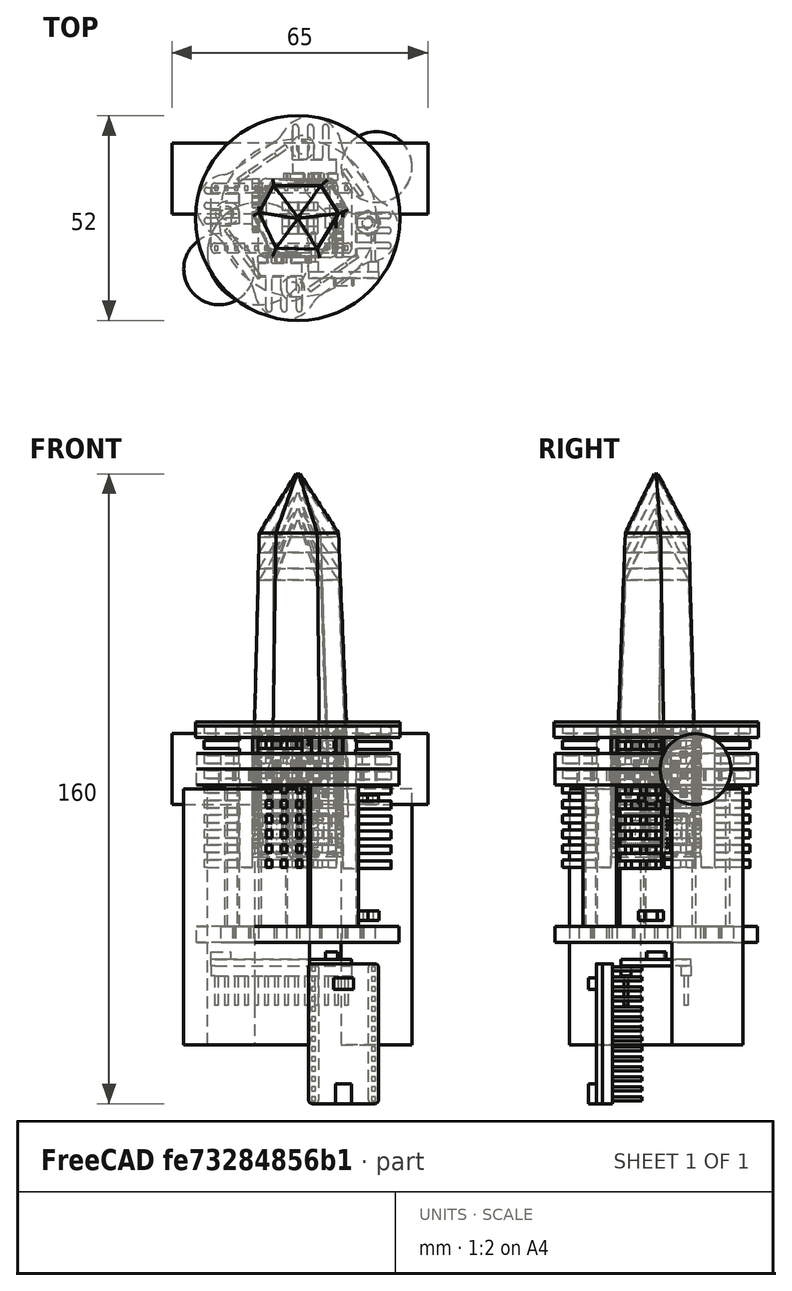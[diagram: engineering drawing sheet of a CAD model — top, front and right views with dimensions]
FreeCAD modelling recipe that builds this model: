
FCSTD DOCUMENT  (FreeCAD 0.18R16093 (Git))
Label: magic_crystal
License: All rights reserved
LicenseURL: http://en.wikipedia.org/wiki/All_rights_reserved
objects: PartDesign::Body×41, Sketcher::SketchObject×25, PartDesign::FeatureBase×25, TechDraw::DrawViewPart×18, PartDesign::Pad×13, App::Part×12, Part::Feature×11, TechDraw::DrawSVGTemplate×10, TechDraw::DrawPage×10, PartDesign::Pocket×6, PartDesign::Hole×6, PartDesign::PolarPattern×6, PartDesign::ShapeBinder×4, PartDesign::Boolean×4, App::DocumentObjectGroup×3, PartDesign::Mirrored×2, TechDraw::DrawViewDimension×2, Spreadsheet::Sheet×1, PartDesign::Fillet×1
note: 169 computed .brp shape members not serialized (recipe doc carries the construction recipe); baked Part::Feature solids carry a one-line shape summary decoded from their .brp

FEATURE [Part::Feature] COMPOUND176_copy_mp_cp001  label="LEDBoard_4x4_HD_simplified1"
  Placement = pos=(11.3,-4,0) rot=(0.57735,0.57735,-0.57735;2.0944rad)
  shape: bbox 2.65 x 13.6 x 33 mm, 1697 faces, 167 solids (baked)
FEATURE [Sketcher::SketchObject] Sketch003  label="lightguide_layer1_Sketch"
  MapMode = 5
  Placement = pos=(0,0,0) rot=(1,0,0;1.5708rad)
  Support = -> [XZ_Plane001]
  expr: Constraints[89] = data.led_height
  expr: Constraints[1] = data.lightguide_top_length
  expr: Constraints[86] = data.led_height
  expr: Constraints[20] = data.led_offset
  expr: Constraints[15] = data.led_pos_0
  expr: Constraints[21] = 5
  expr: Constraints[19] = data.led_offset
  expr: Constraints[18] = data.led_offset
  expr: Constraints[14] = data.led_height
  sketch-geometry (40):
    g0: LineSegment StartX=-4 StartY=0 StartZ=0 EndX=4 EndY=0 EndZ=0
    g1: LineSegment StartX=4.5 StartY=-8 StartZ=0 EndX=5 EndY=-8 EndZ=0
    g2: LineSegment StartX=5 StartY=-8 StartZ=0 EndX=5 EndY=-10 EndZ=0
    g3: LineSegment StartX=5 StartY=-10 StartZ=0 EndX=4.5 EndY=-10 EndZ=0
    g4: ArcOfCircle CenterX=4.5 CenterY=-7.9 CenterZ=0 NormalX=0 NormalY=0 NormalZ=1 AngleXU=0 Radius=2.1 StartAngle=3.14159 EndAngle=4.71239
    g5: ArcOfCircle CenterX=4.5 CenterY=-7.5 CenterZ=0 NormalX=0 NormalY=0 NormalZ=1 AngleXU=0 Radius=0.5 StartAngle=3.14159 EndAngle=4.71239
    g6: LineSegment StartX=2.4 StartY=-7.9 StartZ=0 EndX=2.4 EndY=-2 EndZ=0
    g7: LineSegment StartX=4 StartY=-7.5 StartZ=0 EndX=4 EndY=0 EndZ=0
    g8: GeomPoint X=5 Y=-9 Z=0
    g9: GeomPoint X=5 Y=-14 Z=0
    g10: GeomPoint X=5 Y=-19 Z=0
    g11: GeomPoint X=5 Y=-24 Z=0
    g12: LineSegment StartX=4.5 StartY=-13 StartZ=0 EndX=5 EndY=-13 EndZ=0
    g13: LineSegment StartX=5 StartY=-13 StartZ=0 EndX=5 EndY=-15 EndZ=0
    g14: LineSegment StartX=5 StartY=-15 StartZ=0 EndX=4.5 EndY=-15 EndZ=0
    g15: ArcOfCircle CenterX=4.5 CenterY=-10.6 CenterZ=0 NormalX=0 NormalY=0 NormalZ=1 AngleXU=0 Radius=4.4 StartAngle=3.14159 EndAngle=4.71239
    g16: ArcOfCircle CenterX=4.5 CenterY=-10.7 CenterZ=0 NormalX=0 NormalY=0 NormalZ=1 AngleXU=0 Radius=2.3 StartAngle=3.14159 EndAngle=4.71239
    g17: LineSegment StartX=0.1 StartY=-10.6 StartZ=0 EndX=0.1 EndY=-2 EndZ=0
    g18: LineSegment StartX=2.2 StartY=-10.7 StartZ=0 EndX=2.2 EndY=-2 EndZ=0
    g19: ArcOfCircle CenterX=2.3 CenterY=-2 CenterZ=0 NormalX=0 NormalY=0 NormalZ=1 AngleXU=0 Radius=0.1 StartAngle=-9e-16 EndAngle=3.14159
    g20: LineSegment StartX=4 StartY=-18 StartZ=0 EndX=5 EndY=-18 EndZ=0
    g21: LineSegment StartX=5 StartY=-18 StartZ=0 EndX=5 EndY=-20 EndZ=0
    g22: LineSegment StartX=5 StartY=-20 StartZ=0 EndX=4 EndY=-20 EndZ=0
    g23: ArcOfCircle CenterX=4 CenterY=-13.8 CenterZ=0 NormalX=0 NormalY=0 NormalZ=1 AngleXU=0 Radius=6.2 StartAngle=3.14159 EndAngle=4.71239
    g24: ArcOfCircle CenterX=4 CenterY=-13.9 CenterZ=0 NormalX=0 NormalY=0 NormalZ=1 AngleXU=0 Radius=4.1 StartAngle=3.14159 EndAngle=4.71239
    g25: LineSegment StartX=-2.2 StartY=-13.8 StartZ=0 EndX=-2.2 EndY=-2 EndZ=0
    g26: LineSegment StartX=-0.1 StartY=-13.9 StartZ=0 EndX=-0.1 EndY=-2 EndZ=0
    g27: ArcOfCircle CenterX=0 CenterY=-2 CenterZ=0 NormalX=0 NormalY=0 NormalZ=1 AngleXU=0 Radius=0.1 StartAngle=-9e-16 EndAngle=3.14159
    g28: LineSegment StartX=4 StartY=-23 StartZ=0 EndX=5 EndY=-23 EndZ=0
    g29: LineSegment StartX=5 StartY=-23 StartZ=0 EndX=5 EndY=-25 EndZ=0
    g30: LineSegment StartX=5 StartY=-25 StartZ=0 EndX=4 EndY=-25 EndZ=0
    g31: ArcOfCircle CenterX=4 CenterY=-17 CenterZ=0 NormalX=0 NormalY=0 NormalZ=1 AngleXU=0 Radius=8 StartAngle=3.14159 EndAngle=4.71239
    g32: ArcOfCircle CenterX=4 CenterY=-16.6 CenterZ=0 NormalX=0 NormalY=0 NormalZ=1 AngleXU=0 Radius=6.4 StartAngle=3.14159 EndAngle=4.71239
    g33: LineSegment StartX=-4 StartY=-17 StartZ=0 EndX=-4 EndY=0 EndZ=0
    g34: LineSegment StartX=-2.4 StartY=-16.6 StartZ=0 EndX=-2.4 EndY=-2 EndZ=0
    g35: ArcOfCircle CenterX=-2.3 CenterY=-2 CenterZ=0 NormalX=0 NormalY=0 NormalZ=1 AngleXU=0 Radius=0.1 StartAngle=-9e-16 EndAngle=3.14159
    g36: LineSegment [constr] StartX=-4 StartY=-2 StartZ=0 EndX=-2.3 EndY=-2 EndZ=0
    g37: LineSegment [constr] StartX=-2.3 StartY=-2 StartZ=0 EndX=0 EndY=-2 EndZ=0
    g38: LineSegment [constr] StartX=0 StartY=-2 StartZ=0 EndX=2.3 EndY=-2 EndZ=0
    g39: LineSegment [constr] StartX=2.3 StartY=-2 StartZ=0 EndX=4 EndY=-2 EndZ=0
  constraints (100):
    c: Horizontal(g0)
    c: DistanceX(g0,g0) = 8
    c: Symmetric(g0,g0,g-1)
    c: Horizontal(g1)
    c: Coincident(g1,g2)
    c: Vertical(g2)
    c: Coincident(g2,g3)
    c: Horizontal(g3)
    c: Vertical(g6)
    c: Vertical(g7)
    c: Tangent(g5,g7) = 1.5708
    c: Tangent(g5,g1) = -1.5708
    c: Tangent(g4,g6) = 1.5708
    c: Tangent(g3,g4) = 1.5708
    c: DistanceY(g2,g2) = 2
    c: DistanceY(g8,g-1) = 9
    c: Symmetric(g2,g2,g8)
    c: Radius(g5) = 0.5
    c: DistanceY(g9,g8) = 5
    c: DistanceY(g10,g9) = 5
    c: DistanceY(g11,g10) = 5
    c: DistanceX(g8) = 5
    c: Coincident(g7,g0)
    c: PointOnObject(g9,g2)
    c: PointOnObject(g10,g2)
    c: PointOnObject(g11,g2)
    c: Horizontal(g12)
    c: Coincident(g12,g13)
    c: Vertical(g13)
    c: Coincident(g13,g14)
    c: Horizontal(g14)
    c: Vertical(g17)
    c: Vertical(g18)
    c: Tangent(g16,g18) = 1.5708
    c: Tangent(g16,g12) = -1.5708
    c: Tangent(g15,g17) = 1.5708
    c: Tangent(g14,g15) = 1.5708
    c: Symmetric(g13,g13,g9)
    c: Tangent(g6,g19) = -1.5708
    c: Radius(g19) = 0.1
    c: Tangent(g18,g19) = 1.5708
    c: Horizontal(g20)
    c: Coincident(g20,g21)
    c: Vertical(g21)
    c: Coincident(g21,g22)
    c: Horizontal(g22)
    c: Vertical(g25)
    c: Vertical(g26)
    c: Tangent(g24,g26) = 1.5708
    c: Tangent(g24,g20) = -1.5708
    c: Tangent(g23,g25) = 1.5708
    c: Tangent(g22,g23) = 1.5708
    c: Equal(g19,g27) = 0.1
    c: Tangent(g26,g27) = 1.5708
    c: Horizontal(g28)
    c: Coincident(g28,g29)
    c: Vertical(g29)
    c: Coincident(g29,g30)
    c: Horizontal(g30)
    c: Vertical(g33)
    c: Vertical(g34)
    c: Tangent(g32,g34) = 1.5708
    c: Tangent(g32,g28) = -1.5708
    c: Tangent(g31,g33) = 1.5708
    c: Tangent(g30,g31) = 1.5708
    c: Tangent(g34,g35) = 1.5708
    c: Symmetric(g21,g21,g10)
    c: Tangent(g35,g25) = -1.5708
    c: Tangent(g27,g17) = -1.5708
    c: Equal(g2,g21)
    c: Symmetric(g29,g29,g11)
    c: Coincident(g33,g0)
    c: Horizontal(g36)
    c: Coincident(g36,g37)
    c: Horizontal(g37)
    c: Coincident(g37,g38)
    c: Horizontal(g38)
    c: Coincident(g38,g39)
    c: Horizontal(g39)
    c: PointOnObject(g39,g7)
    c: PointOnObject(g36,g33)
    c: Coincident(g36,g35)
    c: Coincident(g27,g37)
    c: Coincident(g19,g38)
    c: DistanceY(g39,g-1) = 2
    c: DistanceX(g4,g5) = 1.6
    c: DistanceY(g29,g29) = 2
    c: Equal(g35,g19)
    c: DistanceX(g36,g34) = 1.6
    c: DistanceY(g13,g13) = 2
    c: PointOnObject(g27,g-2)
    c: DistanceX(g28,g28) = 1
    c: DistanceX(g20,g20) = 1
    c: Equal(g22,g20)
    c: Equal(g12,g14)
    c: Equal(g30,g28)
    c: Equal(g1,g3)
    c: DistanceX(g12,g12) = 0.5
    c: DistanceX(g1,g1) = 0.5
    c: DistanceX(g17,g18) = 2.1
FEATURE [PartDesign::Pad] Pad
  Length = 2
  Length2 = 100
  Midplane = true
  Placement = pos=(0,0,0) rot=(1,0,0;1.5708rad)
  Profile = -> Sketch003
  Refine = true
  Type = 0
  expr: Length = data.acrylglass_tchickness
FEATURE [PartDesign::Body] Body001  label="lightguide_layer1_Body"
  Group = -> [Sketch003,Pad]
  Origin = -> Origin001
  Placement = pos=(0,3,0) rot=(0,0,1;0rad)
  Tip = -> Pad
FEATURE [Sketcher::SketchObject] Sketch005  label="crystal_contour_simple_Sketch"
  MapMode = 5
  Support = -> [XY_Plane003]
  sketch-geometry (7):
    g0: LineSegment StartX=5 StartY=-8.66025 StartZ=0 EndX=10 EndY=-1.8e-15 EndZ=0
    g1: LineSegment StartX=10 StartY=-1.8e-15 StartZ=0 EndX=5 EndY=8.66025 EndZ=0
    g2: LineSegment StartX=5 StartY=8.66025 StartZ=0 EndX=-5 EndY=8.66025 EndZ=0
    g3: LineSegment StartX=-5 StartY=8.66025 StartZ=0 EndX=-10 EndY=1.8e-15 EndZ=0
    g4: LineSegment StartX=-10 StartY=1.8e-15 StartZ=0 EndX=-5 EndY=-8.66025 EndZ=0
    g5: LineSegment StartX=-5 StartY=-8.66025 StartZ=0 EndX=5 EndY=-8.66025 EndZ=0
    g6: Circle [constr] CenterX=0 CenterY=0 CenterZ=0 NormalX=0 NormalY=0 NormalZ=1 AngleXU=0 Radius=10
  constraints (16):
    c: Coincident(g0,g1)
    c: Coincident(g1,g2)
    c: Coincident(g2,g3)
    c: Coincident(g3,g4)
    c: Coincident(g4,g5)
    c: Coincident(g5,g0)
    c: Equal(g0, g1-g5) x5
    c: PointOnObject(g0,g6)
    c: PointOnObject(g1,g6)
    c: PointOnObject(g2,g6)
    c: PointOnObject(g3,g6)
    c: PointOnObject(g4,g6)
    c: PointOnObject(g5,g6)
    c: Coincident(g6,g-1)
    c: Horizontal(g5)
    c: Radius(g6) = 10
FEATURE [Part::Feature] COMPOUND176_copy_mp_cp002  label="LEDBoard_4x4_HD_simplified2"
  Placement = pos=(-4.1,-11.3,0) rot=(0.707107,0,-0.707107;3.14159rad)
  shape: bbox 13.6 x 2.65 x 33 mm, 1697 faces, 167 solids (baked)
FEATURE [Part::Feature] COMPOUND176_copy_mp_cp003  label="LEDBoard_4x4_HD_simplified3"
  Placement = pos=(-11.5,4,0) rot=(0.57735,-0.57735,-0.57735;4.18879rad)
  shape: bbox 2.65 x 13.6 x 33 mm, 1697 faces, 167 solids (baked)
FEATURE [Part::Feature] COMPOUND176_copy_mp_cp004  label="LEDBoard_4x4_HD_simplified4"
  Placement = pos=(4,11.3,0) rot=(0,1,0;1.5708rad)
  shape: bbox 13.6 x 2.65 x 33 mm, 1697 faces, 167 solids (baked)
FEATURE [Sketcher::SketchObject] Sketch006  label="lightguide_place1_Sketch"
  AttachmentOffset = pos=(4,-3,0) rot=(0,0,1;0rad)
  MapMode = 5
  Placement = pos=(4,-3,0) rot=(0,0,1;0rad)
  Support = -> [XY_Plane003]
  sketch-geometry (4):
    g0: LineSegment StartX=-3.15 StartY=4 StartZ=0 EndX=3.15 EndY=4 EndZ=0
    g1: LineSegment StartX=3.15 StartY=4 StartZ=0 EndX=3.15 EndY=-4 EndZ=0
    g2: LineSegment StartX=3.15 StartY=-4 StartZ=0 EndX=-3.15 EndY=-4 EndZ=0
    g3: LineSegment StartX=-3.15 StartY=-4 StartZ=0 EndX=-3.15 EndY=4 EndZ=0
  constraints (11):
    c: Coincident(g0,g1)
    c: Coincident(g1,g2)
    c: Coincident(g2,g3)
    c: Coincident(g3,g0)
    c: Horizontal(g0)
    c: Horizontal(g2)
    c: Vertical(g1)
    c: Vertical(g3)
    c: DistanceX(g0,g0) = 6.3
    c: Symmetric(g0,g2,g-1)
    c: DistanceY(g1,g1) = 8
FEATURE [Sketcher::SketchObject] Sketch007  label="lightguide_place2_Sketch"
  AttachmentOffset = pos=(-3.15,-3.85,0) rot=(0,0,1;1.5708rad)
  MapMode = 5
  Placement = pos=(-3.15,-3.85,0) rot=(0,0,1;1.5708rad)
  Support = -> [XY_Plane003]
  sketch-geometry (4):
    g0: LineSegment StartX=-3.15 StartY=4 StartZ=0 EndX=3.15 EndY=4 EndZ=0
    g1: LineSegment StartX=3.15 StartY=4 StartZ=0 EndX=3.15 EndY=-4 EndZ=0
    g2: LineSegment StartX=3.15 StartY=-4 StartZ=0 EndX=-3.15 EndY=-4 EndZ=0
    g3: LineSegment StartX=-3.15 StartY=-4 StartZ=0 EndX=-3.15 EndY=4 EndZ=0
  constraints (11):
    c: Coincident(g0,g1)
    c: Coincident(g1,g2)
    c: Coincident(g2,g3)
    c: Coincident(g3,g0)
    c: Horizontal(g0)
    c: Horizontal(g2)
    c: Vertical(g1)
    c: Vertical(g3)
    c: DistanceX(g0,g0) = 6.3
    c: Symmetric(g0,g2,g-1)
    c: DistanceY(g3,g3) = 8
FEATURE [Sketcher::SketchObject] Sketch008  label="lightguide_place3_Sketch"
  AttachmentOffset = pos=(-4,3.3,0) rot=(0,0,1;0rad)
  MapMode = 5
  Placement = pos=(-4,3.3,0) rot=(0,0,1;0rad)
  Support = -> [XY_Plane003]
  sketch-geometry (4):
    g0: LineSegment StartX=-3.15 StartY=4 StartZ=0 EndX=3.15 EndY=4 EndZ=0
    g1: LineSegment StartX=3.15 StartY=4 StartZ=0 EndX=3.15 EndY=-4 EndZ=0
    g2: LineSegment StartX=3.15 StartY=-4 StartZ=0 EndX=-3.15 EndY=-4 EndZ=0
    g3: LineSegment StartX=-3.15 StartY=-4 StartZ=0 EndX=-3.15 EndY=4 EndZ=0
  constraints (11):
    c: Coincident(g0,g1)
    c: Coincident(g1,g2)
    c: Coincident(g2,g3)
    c: Coincident(g3,g0)
    c: Horizontal(g0)
    c: Horizontal(g2)
    c: Vertical(g1)
    c: Vertical(g3)
    c: DistanceX(g0,g0) = 6.3
    c: Symmetric(g0,g2,g-1)
    c: DistanceY(g1,g1) = 8
FEATURE [Sketcher::SketchObject] Sketch009  label="lightguide_place4_Sketch"
  AttachmentOffset = pos=(3.15,4.15,0) rot=(0,0,1;0rad)
  MapMode = 5
  Placement = pos=(3.15,4.15,0) rot=(0,0,1;0rad)
  Support = -> [XY_Plane003]
  sketch-geometry (4):
    g0: LineSegment StartX=-4 StartY=3.15 StartZ=0 EndX=4 EndY=3.15 EndZ=0
    g1: LineSegment StartX=4 StartY=3.15 StartZ=0 EndX=4 EndY=-3.15 EndZ=0
    g2: LineSegment StartX=4 StartY=-3.15 StartZ=0 EndX=-4 EndY=-3.15 EndZ=0
    g3: LineSegment StartX=-4 StartY=-3.15 StartZ=0 EndX=-4 EndY=3.15 EndZ=0
  constraints (11):
    c: Coincident(g0,g1)
    c: Coincident(g1,g2)
    c: Coincident(g2,g3)
    c: Coincident(g3,g0)
    c: Horizontal(g0)
    c: Horizontal(g2)
    c: Vertical(g1)
    c: Vertical(g3)
    c: DistanceX(g0,g0) = 8
    c: Symmetric(g0,g2,g-1)
    c: DistanceY(g1,g1) = 6.3
FEATURE [Spreadsheet::Sheet] Spreadsheet  label="data"
  cells = A1=acrylglass_thickness; B1(acrylglass_tchickness)=2; A2=acrylglass_tchickness2; B2(acrylglass_tchickness2)=2; A3=led_height; B3(led_height)=2; A4=led_offset; B4(led_offset)=5; A5=led_pos_0; B5(led_pos_0)==led_pos_1 + led_offset / 2; A6=led_pos_1; B6(led_pos_1)=6.5; A8=crystal_mounting_fit_offset; B8(crystal_mounting_fit_offset)=-1; A10=lightblocker_side_height; B10(lightblocker_side_height)==data.wood_thickness + 36 + data.wood_thickness; A12=mounting_outline_radius; B12(mounting_outline_radius)=26; A15=lightguide_top_length; B15(lightguide_top_length)=8; A16=lightguide_min_radius; B16(lightguide_min_radius)=0.5; A20=wood_thickness; B20(wood_thickness)=4; A21=wood2_thickness; B21(wood2_thickness)=1; A22=wood3_thickness; B22(wood3_thickness)=3
FEATURE [Sketcher::SketchObject] Sketch010
  MapMode = 5
  Support = -> [XY_Plane007]
  sketch-geometry (1):
    g0: Circle CenterX=0 CenterY=0 CenterZ=0 NormalX=0 NormalY=0 NormalZ=1 AngleXU=0 Radius=20
  constraints (2):
    c: Coincident(g0,g-1)
    c: Radius(g0) = 20
FEATURE [PartDesign::Pad] Pad002
  Length = 4
  Length2 = 100
  Profile = -> Sketch010
  Reversed = true
  Type = 0
FEATURE [Sketcher::SketchObject] Sketch011  label="lightguide_layer2_Sketch"
  MapMode = 5
  Placement = pos=(0,0,0) rot=(1,0,0;1.5708rad)
  Support = -> [XZ_Plane008]
  expr: Constraints[89] = data.led_height
  expr: Constraints[1] = data.lightguide_top_length
  expr: Constraints[86] = data.led_height
  expr: Constraints[20] = data.led_offset
  expr: Constraints[15] = data.led_pos_1
  expr: Constraints[21] = 5
  expr: Constraints[19] = data.led_offset
  expr: Constraints[18] = data.led_offset
  expr: Constraints[14] = data.led_height
  sketch-geometry (40):
    g0: LineSegment StartX=-4 StartY=0 StartZ=0 EndX=4 EndY=0 EndZ=0
    g1: LineSegment StartX=4.5 StartY=-5.5 StartZ=0 EndX=5 EndY=-5.5 EndZ=0
    g2: LineSegment StartX=5 StartY=-5.5 StartZ=0 EndX=5 EndY=-7.5 EndZ=0
    g3: LineSegment StartX=5 StartY=-7.5 StartZ=0 EndX=4.5 EndY=-7.5 EndZ=0
    g4: ArcOfCircle CenterX=4.5 CenterY=-5.5 CenterZ=0 NormalX=0 NormalY=0 NormalZ=1 AngleXU=0 Radius=2 StartAngle=3.14159 EndAngle=4.71239
    g5: ArcOfCircle CenterX=4.5 CenterY=-5 CenterZ=0 NormalX=0 NormalY=0 NormalZ=1 AngleXU=0 Radius=0.5 StartAngle=3.14159 EndAngle=4.71239
    g6: LineSegment StartX=2.5 StartY=-5.5 StartZ=0 EndX=2.5 EndY=-2 EndZ=0
    g7: LineSegment StartX=4 StartY=-5 StartZ=0 EndX=4 EndY=0 EndZ=0
    g8: GeomPoint X=5 Y=-6.5 Z=0
    g9: GeomPoint X=5 Y=-11.5 Z=0
    g10: GeomPoint X=5 Y=-16.5 Z=0
    g11: GeomPoint X=5 Y=-21.5 Z=0
    g12: LineSegment StartX=4.5 StartY=-10.5 StartZ=0 EndX=5 EndY=-10.5 EndZ=0
    g13: LineSegment StartX=5 StartY=-10.5 StartZ=0 EndX=5 EndY=-12.5 EndZ=0
    g14: LineSegment StartX=5 StartY=-12.5 StartZ=0 EndX=4.5 EndY=-12.5 EndZ=0
    g15: ArcOfCircle CenterX=4.5 CenterY=-8.1 CenterZ=0 NormalX=0 NormalY=0 NormalZ=1 AngleXU=0 Radius=4.4 StartAngle=3.14159 EndAngle=4.71239
    g16: ArcOfCircle CenterX=4.5 CenterY=-8.3 CenterZ=0 NormalX=0 NormalY=0 NormalZ=1 AngleXU=0 Radius=2.2 StartAngle=3.14159 EndAngle=4.71239
    g17: LineSegment StartX=0.1 StartY=-8.1 StartZ=0 EndX=0.1 EndY=-2 EndZ=0
    g18: LineSegment StartX=2.3 StartY=-8.3 StartZ=0 EndX=2.3 EndY=-2 EndZ=0
    g19: ArcOfCircle CenterX=2.4 CenterY=-2 CenterZ=0 NormalX=0 NormalY=0 NormalZ=1 AngleXU=0 Radius=0.1 StartAngle=8e-16 EndAngle=3.14159
    g20: LineSegment StartX=4 StartY=-15.5 StartZ=0 EndX=5 EndY=-15.5 EndZ=0
    g21: LineSegment StartX=5 StartY=-15.5 StartZ=0 EndX=5 EndY=-17.5 EndZ=0
    g22: LineSegment StartX=5 StartY=-17.5 StartZ=0 EndX=4 EndY=-17.5 EndZ=0
    g23: ArcOfCircle CenterX=4 CenterY=-11.2 CenterZ=0 NormalX=0 NormalY=0 NormalZ=1 AngleXU=0 Radius=6.3 StartAngle=3.14159 EndAngle=4.71239
    g24: ArcOfCircle CenterX=4 CenterY=-11.4 CenterZ=0 NormalX=0 NormalY=0 NormalZ=1 AngleXU=0 Radius=4.1 StartAngle=3.14159 EndAngle=4.71239
    g25: LineSegment StartX=-2.3 StartY=-11.2 StartZ=0 EndX=-2.3 EndY=-2 EndZ=0
    g26: LineSegment StartX=-0.1 StartY=-11.4 StartZ=0 EndX=-0.1 EndY=-2 EndZ=0
    g27: ArcOfCircle CenterX=0 CenterY=-2 CenterZ=0 NormalX=0 NormalY=0 NormalZ=1 AngleXU=0 Radius=0.1 StartAngle=-9e-16 EndAngle=3.14159
    g28: LineSegment StartX=4 StartY=-20.5 StartZ=0 EndX=5 EndY=-20.5 EndZ=0
    g29: LineSegment StartX=5 StartY=-20.5 StartZ=0 EndX=5 EndY=-22.5 EndZ=0
    g30: LineSegment StartX=5 StartY=-22.5 StartZ=0 EndX=4 EndY=-22.5 EndZ=0
    g31: ArcOfCircle CenterX=4 CenterY=-14.5 CenterZ=0 NormalX=0 NormalY=0 NormalZ=1 AngleXU=0 Radius=8 StartAngle=3.14159 EndAngle=4.71239
    g32: ArcOfCircle CenterX=4 CenterY=-14 CenterZ=0 NormalX=0 NormalY=0 NormalZ=1 AngleXU=0 Radius=6.5 StartAngle=3.14159 EndAngle=4.71239
    g33: LineSegment StartX=-4 StartY=-14.5 StartZ=0 EndX=-4 EndY=0 EndZ=0
    g34: LineSegment StartX=-2.5 StartY=-14 StartZ=0 EndX=-2.5 EndY=-2 EndZ=0
    g35: ArcOfCircle CenterX=-2.4 CenterY=-2 CenterZ=0 NormalX=0 NormalY=0 NormalZ=1 AngleXU=0 Radius=0.1 StartAngle=-9e-16 EndAngle=3.14159
    g36: LineSegment [constr] StartX=-4 StartY=-2 StartZ=0 EndX=-2.4 EndY=-2 EndZ=0
    g37: LineSegment [constr] StartX=-2.4 StartY=-2 StartZ=0 EndX=0 EndY=-2 EndZ=0
    g38: LineSegment [constr] StartX=0 StartY=-2 StartZ=0 EndX=2.4 EndY=-2 EndZ=0
    g39: LineSegment [constr] StartX=2.4 StartY=-2 StartZ=0 EndX=4 EndY=-2 EndZ=0
  constraints (99):
    c: Horizontal(g0)
    c: DistanceX(g0,g0) = 8
    c: Symmetric(g0,g0,g-1)
    c: Horizontal(g1)
    c: Coincident(g1,g2)
    c: Vertical(g2)
    c: Coincident(g2,g3)
    c: Horizontal(g3)
    c: Vertical(g6)
    c: Vertical(g7)
    c: Tangent(g5,g7) = 1.5708
    c: Tangent(g5,g1) = -1.5708
    c: Tangent(g4,g6) = 1.5708
    c: Tangent(g3,g4) = 1.5708
    c: DistanceY(g2,g2) = 2
    c: DistanceY(g8,g-1) = 6.5
    c: Symmetric(g2,g2,g8)
    c: Radius(g5) = 0.5
    c: DistanceY(g9,g8) = 5
    c: DistanceY(g10,g9) = 5
    c: DistanceY(g11,g10) = 5
    c: DistanceX(g8) = 5
    c: Coincident(g7,g0)
    c: PointOnObject(g9,g2)
    c: PointOnObject(g10,g2)
    c: PointOnObject(g11,g2)
    c: Horizontal(g12)
    c: Coincident(g12,g13)
    c: Vertical(g13)
    c: Coincident(g13,g14)
    c: Horizontal(g14)
    c: Vertical(g17)
    c: Vertical(g18)
    c: Tangent(g16,g18) = 1.5708
    c: Tangent(g16,g12) = -1.5708
    c: Tangent(g15,g17) = 1.5708
    c: Tangent(g14,g15) = 1.5708
    c: Symmetric(g13,g13,g9)
    c: Tangent(g6,g19) = -1.5708
    c: Radius(g19) = 0.1
    c: Tangent(g18,g19) = 1.5708
    c: Horizontal(g20)
    c: Coincident(g20,g21)
    c: Vertical(g21)
    c: Coincident(g21,g22)
    c: Horizontal(g22)
    c: Vertical(g25)
    c: Vertical(g26)
    c: Tangent(g24,g26) = 1.5708
    c: Tangent(g24,g20) = -1.5708
    c: Tangent(g23,g25) = 1.5708
    c: Tangent(g22,g23) = 1.5708
    c: Equal(g19,g27) = 0.1
    c: Tangent(g26,g27) = 1.5708
    c: Horizontal(g28)
    c: Coincident(g28,g29)
    c: Vertical(g29)
    c: Coincident(g29,g30)
    c: Horizontal(g30)
    c: Vertical(g33)
    c: Vertical(g34)
    c: Tangent(g32,g34) = 1.5708
    c: Tangent(g32,g28) = -1.5708
    c: Tangent(g31,g33) = 1.5708
    c: Tangent(g30,g31) = 1.5708
    c: Tangent(g34,g35) = 1.5708
    c: Symmetric(g21,g21,g10)
    c: Tangent(g35,g25) = -1.5708
    c: Tangent(g27,g17) = -1.5708
    c: Equal(g2,g21)
    c: Symmetric(g29,g29,g11)
    c: Coincident(g33,g0)
    c: Horizontal(g36)
    c: Coincident(g36,g37)
    c: Horizontal(g37)
    c: Coincident(g37,g38)
    c: Horizontal(g38)
    c: Coincident(g38,g39)
    c: Horizontal(g39)
    c: PointOnObject(g39,g7)
    c: PointOnObject(g36,g33)
    c: Coincident(g36,g35)
    c: Coincident(g27,g37)
    c: Coincident(g19,g38)
    c: DistanceY(g39,g-1) = 2
    c: DistanceX(g4,g5) = 1.5
    c: DistanceY(g29,g29) = 2
    c: Equal(g35,g19)
    c: DistanceX(g36,g34) = 1.5
    c: DistanceY(g13,g13) = 2
    c: PointOnObject(g27,g-2)
    c: DistanceX(g28,g28) = 1
    c: DistanceX(g20,g20) = 1
    c: Equal(g22,g20)
    c: Equal(g12,g14)
    c: Equal(g30,g28)
    c: Equal(g1,g3)
    c: DistanceX(g12,g12) = 0.5
    c: DistanceX(g1,g1) = 0.5
FEATURE [PartDesign::Pad] Pad003
  Length = 2
  Length2 = 100
  Midplane = true
  Placement = pos=(0,0,0) rot=(1,0,0;1.5708rad)
  Profile = -> Sketch011
  Refine = true
  Type = 0
  expr: Length = data.acrylglass_tchickness2
FEATURE [PartDesign::Body] Body005  label="lightguide_layer2_Body"
  Group = -> [Sketch011,Pad003]
  Origin = -> Origin008
  Placement = pos=(0,1,0) rot=(0,0,1;0rad)
  Tip = -> Pad003
FEATURE [PartDesign::FeatureBase] Clone
  BaseFeature = -> Body001
  Placement = pos=(0,3,0) rot=(0,0,1;0rad)
FEATURE [PartDesign::Body] Body006  label="lightguide_layer3_Body"
  BaseFeature = -> Body001
  Group = -> [Clone]
  Origin = -> Origin009
  Placement = pos=(0,-4,0) rot=(0,0,1;0rad)
  Tip = -> Clone
FEATURE [PartDesign::FeatureBase] Clone001
  BaseFeature = -> Body005
  Placement = pos=(0,1,0) rot=(0,0,1;0rad)
FEATURE [PartDesign::Body] Body007  label="lightguide_layer4_Body"
  BaseFeature = -> Body005
  Group = -> [Clone001]
  Origin = -> Origin010
  Placement = pos=(0,-4,0) rot=(0,0,1;0rad)
  Tip = -> Clone001
FEATURE [App::Part] Part  label="lightguide_place1_Part"
  Group = -> [Body001,Body005,Body006,Body007]
  Origin = -> Origin004
  Placement = pos=(4,-4,0) rot=(0,0,1;0rad)
FEATURE [TechDraw::DrawSVGTemplate] Template
  Height = 210
  Orientation = 1
  Width = 297
FEATURE [TechDraw::DrawSVGTemplate] Template001
  Height = 210
  Orientation = 1
  Width = 297
FEATURE [TechDraw::DrawViewPart] View
  CoarseView = false
  Direction = (0,-1,0)
  Focus = 100
  HardHidden = false
  IsoCount = 0
  IsoHidden = false
  IsoVisible = false
  LockPosition = false
  Perspective = false
  Rotation = 0
  ScaleType = 0
  SeamHidden = false
  SeamVisible = false
  SmoothHidden = false
  SmoothVisible = false
  Source = -> [Body001]
  X = 148.5
  Y = 105
FEATURE [TechDraw::DrawPage] Page  label="lightguide_layer1_Page"
  KeepUpdated = true
  ProjectionType = 0
  Template = -> Template
  Views = -> [View]
FEATURE [TechDraw::DrawViewPart] View001
  CoarseView = false
  Direction = (0,-1,0)
  Focus = 100
  HardHidden = false
  IsoCount = 0
  IsoHidden = false
  IsoVisible = false
  LockPosition = false
  Perspective = false
  Rotation = 0
  ScaleType = 0
  SeamHidden = false
  SeamVisible = false
  SmoothHidden = false
  SmoothVisible = false
  Source = -> [Body005]
  X = 148.5
  Y = 105
FEATURE [TechDraw::DrawPage] Page001  label="lightguide_layer2_Page"
  KeepUpdated = true
  ProjectionType = 0
  Template = -> Template001
  Views = -> [View001]
FEATURE [App::DocumentObjectGroup] Group  label="lightguide_export"
  Group = -> [Page,Page001]
FEATURE [Sketcher::SketchObject] Sketch012  label="lightguide_place1_4_Sketch"
  MapMode = 5
  Support = -> [XY_Plane003]
  expr: Constraints[10] = data.lightguide_top_length + data.acrylglass_tchickness * 2 + data.acrylglass_tchickness2 * 2
  sketch-geometry (4):
    g0: LineSegment StartX=-8 StartY=8 StartZ=0 EndX=8 EndY=8 EndZ=0
    g1: LineSegment StartX=8 StartY=8 StartZ=0 EndX=8 EndY=-8 EndZ=0
    g2: LineSegment StartX=8 StartY=-8 StartZ=0 EndX=-8 EndY=-8 EndZ=0
    g3: LineSegment StartX=-8 StartY=-8 StartZ=0 EndX=-8 EndY=8 EndZ=0
  constraints (11):
    c: Coincident(g0,g1)
    c: Coincident(g1,g2)
    c: Coincident(g2,g3)
    c: Coincident(g3,g0)
    c: Horizontal(g0)
    c: Horizontal(g2)
    c: Vertical(g1)
    c: Vertical(g3)
    c: Symmetric(g2,g0,g-1)
    c: Equal(g0,g1)
    c: DistanceX(g0,g0) = 16
FEATURE [PartDesign::Body] Body003  label="helper_Body"
  Group = -> [Sketch005,Sketch006,Sketch007,Sketch008,Sketch009,Sketch012]
  Origin = -> Origin003
FEATURE [PartDesign::Pocket] Pocket
  BaseFeature = -> Pad002
  Length = 5
  Length2 = 100
  Profile = -> Sketch012
  Type = 0
FEATURE [PartDesign::Body] Body004  label="lightguide_holder_Body"
  Group = -> [Sketch010,Pad002,Pocket]
  Origin = -> Origin007
  Tip = -> Pocket
FEATURE [PartDesign::FeatureBase] Clone002
  BaseFeature = -> Body001
  Placement = pos=(0,3,0) rot=(0,0,1;0rad)
FEATURE [PartDesign::Body] Body008
  BaseFeature = -> Body001
  Group = -> [Clone002]
  Origin = -> Origin012
  Tip = -> Clone002
FEATURE [PartDesign::FeatureBase] Clone003
  BaseFeature = -> Body007
  Placement = pos=(0,-4,0) rot=(0,0,1;0rad)
FEATURE [PartDesign::Body] Body009
  BaseFeature = -> Body007
  Group = -> [Clone003]
  Origin = -> Origin013
  Tip = -> Clone003
FEATURE [App::Part] Part003  label="lightguide_place3_Part"
  Group = -> [Body008,Body009]
  Origin = -> Origin011
  Placement = pos=(-4,4,0) rot=(0,0,1;3.14159rad)
FEATURE [PartDesign::FeatureBase] Clone004
  BaseFeature = -> Body001
  Placement = pos=(0,3,0) rot=(0,0,1;0rad)
FEATURE [PartDesign::Body] Body010
  BaseFeature = -> Body001
  Group = -> [Clone004]
  Origin = -> Origin016
  Tip = -> Clone004
FEATURE [PartDesign::FeatureBase] Clone005
  BaseFeature = -> Body007
  Placement = pos=(0,-4,0) rot=(0,0,1;0rad)
FEATURE [PartDesign::Body] Body011
  BaseFeature = -> Body007
  Group = -> [Clone005]
  Origin = -> Origin017
  Tip = -> Clone005
FEATURE [App::Part] Part004  label="lightguide_place2_Part"
  Group = -> [Body010,Body011]
  Origin = -> Origin014
  Placement = pos=(-4,-4,0) rot=(0,0,1;-1.5708rad)
FEATURE [PartDesign::FeatureBase] Clone006
  BaseFeature = -> Body001
  Placement = pos=(0,3,0) rot=(0,0,1;0rad)
FEATURE [PartDesign::Body] Body012
  BaseFeature = -> Body001
  Group = -> [Clone006]
  Origin = -> Origin018
  Tip = -> Clone006
FEATURE [PartDesign::FeatureBase] Clone007
  BaseFeature = -> Body007
  Placement = pos=(0,-4,0) rot=(0,0,1;0rad)
FEATURE [PartDesign::Body] Body013
  BaseFeature = -> Body007
  Group = -> [Clone007]
  Origin = -> Origin019
  Tip = -> Clone007
FEATURE [App::Part] Part005  label="lightguide_place4_Part"
  Group = -> [Body012,Body013]
  Origin = -> Origin015
  Placement = pos=(4,4,0) rot=(0,0,1;1.5708rad)
FEATURE [App::Part] Part001  label="lightguides_Part"
  Group = -> [Part,Body004,Page001,Page,Group,Part003,Part004,Part005]
  Origin = -> Origin005
FEATURE [Part::Feature] Body002001  label="crystal_detailed_Body_SimpleCopy"
  shape: bbox 24.12 x 20 x 75 mm, 16 faces (baked)
FEATURE [Part::Feature] Body001001  label="crystal_Body_SimpleCopy"
  shape: bbox 24.12 x 20 x 75 mm, 14 faces (baked)
FEATURE [App::Part] Part006  label="crystal_Part"
  Group = -> [Body002001,Body001001]
  Origin = -> Origin
FEATURE [Part::Feature] Body004002  label="HeatSink_Part_Cut_V1_Body1"
  Placement = pos=(11.4,-16.58,-7.25) rot=(0.707107,0,0.707107;3.14159rad)
  shape: bbox 12.3 x 11.2 x 36 mm, 192 faces (baked)
FEATURE [Part::Feature] Body004003  label="HeatSink_Part_Cut_V1_Body002"
  Placement = pos=(-16.9,-11.5,-7) rot=(0.57735,-0.57735,0.57735;2.0944rad)
  shape: bbox 11.2 x 12.3 x 36 mm, 192 faces (baked)
FEATURE [Part::Feature] Body004004  label="HeatSink_Part_Cut_V1_Body003"
  Placement = pos=(-11.5,16.6,-7) rot=(0,-1,0;1.5708rad)
  shape: bbox 12.3 x 11.2 x 36 mm, 192 faces (baked)
FEATURE [Part::Feature] Body004005  label="HeatSink_Part_Cut_V1_Body004"
  Placement = pos=(16.6,11.5,-7) rot=(0.57735,0.57735,0.57735;4.18879rad)
  shape: bbox 11.2 x 12.3 x 36 mm, 192 faces (baked)
FEATURE [Sketcher::SketchObject] Sketch  label="mounting_outline_Sketch"
  MapMode = 5
  Support = -> [XY_Plane023]
  expr: Constraints[24] = data.mounting_outline_radius
  sketch-geometry (9):
    g0: ArcOfCircle CenterX=17.7265 CenterY=-3.12567 CenterZ=0 NormalX=0 NormalY=0 NormalZ=1 AngleXU=0 Radius=8 StartAngle=4.86225 EndAngle=7.35506
    g1: ArcOfCircle CenterX=19.8167 CenterY=-16.9688 CenterZ=0 NormalX=0 NormalY=0 NormalZ=1 AngleXU=0 Radius=6 StartAngle=1.72065 EndAngle=2.18166
    g2: LineSegment StartX=11.0507 StartY=-15.7821 StartZ=0 EndX=16.3752 EndY=-12.0538 EndZ=0
    g3: LineSegment [constr] StartX=0 StartY=0 StartZ=0 EndX=17.7265 EndY=-3.12567 EndZ=0
    g4: LineSegment StartX=19.5103 StartY=5.72625 StartZ=0 EndX=15.7821 EndY=11.0507 EndZ=0
    g5: LineSegment StartX=0 StartY=0 StartZ=0 EndX=15.7821 EndY=11.0507 EndZ=0
    g6: ArcOfCircle CenterX=24.4253 CenterY=9.16771 CenterZ=0 NormalX=0 NormalY=0 NormalZ=1 AngleXU=0 Radius=6 StartAngle=3.75246 EndAngle=4.21347
    g7: LineSegment StartX=0 StartY=0 StartZ=0 EndX=11.0507 EndY=-15.7821 EndZ=0
    g8: LineSegment [constr] StartX=17.7265 StartY=-3.12567 StartZ=0 EndX=25.605 EndY=-4.51485 EndZ=0
  constraints (25):
    c: Tangent(g1,g2) = 1.5708
    c: Tangent(g0,g1) = 1.5708
    c: Coincident(g3,g-1)
    c: Coincident(g3,g0)
    c: Angle(g3,g-1) = 0.174533
    c: Radius(g0) = 8
    c: Distance(g3) = 18
    c: Coincident(g5,g-1)
    c: Coincident(g5,g4)
    c: Tangent(g0,g6) = 1.5708
    c: Tangent(g4,g6) = 1.5708
    c: Perpendicular(g4,g5)
    c: Coincident(g7,g5)
    c: Perpendicular(g5,g7)
    c: Perpendicular(g7,g2) = 1.5708
    c: Coincident(g2,g7)
    c: Equal(g2,g4)
    c: Radius(g6) = 6
    c: Equal(g7,g5)
    c: Equal(g1,g6)
    c: Distance(g4) = 6.5
    c: Coincident(g0,g8)
    c: Perpendicular(g8,g0) = 1.5708
    c: Parallel(g8,g3)
    c: Distance(g8,g5) = 26
FEATURE [PartDesign::Pad] Pad004
  Length = 4
  Length2 = 100
  Profile = -> Sketch
  Type = 0
  expr: Length = data.wood_thickness
FEATURE [PartDesign::Pad] Pad005
  Length = 4
  Length2 = 100
  Offset = 4
  Profile = -> Sketch
  Type = 0
  expr: Length = data.wood_thickness
FEATURE [PartDesign::Pad] Pad006
  Length = 4
  Length2 = 100
  Profile = -> Sketch
  Reversed = true
  Type = 0
  expr: Length = data.wood_thickness
FEATURE [Sketcher::SketchObject] Sketch013
  MapMode = 5
  Support = -> [XY_Plane026]
  sketch-geometry (1):
    g0: Circle CenterX=0 CenterY=0 CenterZ=0 NormalX=0 NormalY=0 NormalZ=1 AngleXU=0 Radius=9
  constraints (2):
    c: Coincident(g0,g-1)
    c: Diameter(g0) = 18
FEATURE [PartDesign::Pad] Pad007
  Length = 65
  Length2 = 100
  Profile = -> Sketch013
  Type = 0
FEATURE [PartDesign::Body] Body004009  label="battery_18650_Body"
  Group = -> [Sketch013,Pad007]
  Origin = -> Origin026
  Tip = -> Pad007
FEATURE [Sketcher::SketchObject] Sketch001
  MapMode = 5
  Support = -> [XY_Plane027]
  sketch-geometry (1):
    g0: Circle CenterX=0 CenterY=0 CenterZ=0 NormalX=0 NormalY=0 NormalZ=1 AngleXU=0 Radius=13
  constraints (2):
    c: Coincident(g0,g-1)
    c: Diameter(g0) = 26
FEATURE [PartDesign::Pad] Pad001
  Length = 65
  Length2 = 100
  Profile = -> Sketch001
  Type = 0
FEATURE [PartDesign::Body] Body004010  label="battery_26650_Body"
  Group = -> [Sketch001,Pad001]
  Origin = -> Origin027
  Tip = -> Pad001
FEATURE [PartDesign::FeatureBase] Clone008
  BaseFeature = -> Body004009
  Placement = pos=(20,13,-70) rot=(0,0,1;0rad)
FEATURE [PartDesign::Body] Body004011  label="battery_18650_clone1_mirrow"
  BaseFeature = -> Body004009
  Group = -> [Clone008]
  Origin = -> Origin031
  Placement = pos=(0,0,0) rot=(0,0,1;3.14159rad)
  Tip = -> Clone008
FEATURE [PartDesign::FeatureBase] Clone009
  BaseFeature = -> Body004009
  Placement = pos=(-32,0,0) rot=(0,1,0;1.5708rad)
FEATURE [PartDesign::Body] Body004012  label="battery_18650_clone3"
  BaseFeature = -> Body004009
  Group = -> [Clone009]
  Origin = -> Origin032
  Placement = pos=(0,-10,0) rot=(0,1,0;0rad)
  Tip = -> Clone009
FEATURE [PartDesign::FeatureBase] Clone010
  BaseFeature = -> Body004009
  Placement = pos=(20,13,-70) rot=(0,0,1;0rad)
FEATURE [PartDesign::Body] Body004013  label="battery_18650_clone1"
  BaseFeature = -> Body004009
  Group = -> [Clone010]
  Origin = -> Origin033
  Tip = -> Clone010
FEATURE [PartDesign::FeatureBase] Clone011
  BaseFeature = -> Body004012
FEATURE [PartDesign::Body] Body004014  label="battery_18650_clone3.1"
  BaseFeature = -> Body004012
  Group = -> [Clone011]
  Origin = -> Origin034
  Placement = pos=(0,10,0) rot=(0,0,1;0rad)
  Tip = -> Clone011
FEATURE [App::Part] Part011  label="batteries_horizontal_Part"
  Group = -> [Body004012,Body004014]
  Origin = -> Origin030
  Placement = pos=(0,0,-70) rot=(0,0,1;0rad)
FEATURE [PartDesign::FeatureBase] Clone012
  BaseFeature = -> Body004010
FEATURE [PartDesign::Body] Body004015  label="battery_26650_clone1"
  BaseFeature = -> Body004010
  Group = -> [Clone012]
  Origin = -> Origin035
  Placement = pos=(10,9,-70) rot=(0,0,1;0rad)
  Tip = -> Clone012
FEATURE [PartDesign::FeatureBase] Clone013
  BaseFeature = -> Body004015
  Placement = pos=(24,16,-70) rot=(0,0,1;0rad)
FEATURE [PartDesign::Body] Body004016  label="battery_26650_clone1_mirrow"
  BaseFeature = -> Body004015
  Group = -> [Clone013]
  Origin = -> Origin036
  Placement = pos=(14,7,0) rot=(0,0,1;3.14159rad)
  Tip = -> Clone013
FEATURE [App::Part] Part010  label="batteries_vertical_Part"
  Group = -> [Body004011,Body004013,Body004015,Body004016]
  Origin = -> Origin029
  Placement = pos=(0,0,-42) rot=(0,0,1;0rad)
FEATURE [App::Part] Part009  label="batteries_Part"
  Group = -> [Part010,Part011,Body004009,Body004010]
  Origin = -> Origin028
FEATURE [Part::Feature] Compound001  label="ItsyBitsy_M4_simplecopy"
  shape: bbox 35.56 x 17.78 x 13.6 mm, 180 faces, 3 solids (baked)
FEATURE [PartDesign::FeatureBase] Clone014
  BaseFeature = -> Compound001
  Placement = pos=(13.4142,-14.4142,-40) rot=(0.57735,0.57735,0.57735;4.18879rad)
FEATURE [PartDesign::Body] Body004017  label="ItsyBitsy_M4_vertical"
  BaseFeature = -> Compound001
  Group = -> [Clone014]
  Origin = -> Origin037
  Placement = pos=(25,-28,-45) rot=(0,0,1;3.14159rad)
  Tip = -> Clone014
FEATURE [PartDesign::FeatureBase] Clone015
  BaseFeature = -> Compound001
FEATURE [PartDesign::Body] Body004018  label="ItsyBitsy_M4_horizontal"
  BaseFeature = -> Compound001
  Group = -> [Clone015]
  Origin = -> Origin038
  Placement = pos=(-22,0,-50) rot=(0,0,1;0rad)
  Tip = -> Clone015
FEATURE [App::Part] Part008  label="electronics_Part"
  Group = -> [Part009,Compound001,Body004017,Body004018]
  Origin = -> Origin025
FEATURE [Sketcher::SketchObject] Sketch014  label="lightblocker_side_profile_Sketch"
  MapMode = 5
  Support = -> [XY_Plane023]
  expr: Constraints[8] = data.wood2_thickness
  sketch-geometry (4):
    g0: LineSegment StartX=9.20845 StartY=14.8813 StartZ=0 EndX=10.0276 EndY=15.4549 EndZ=0
    g1: LineSegment StartX=10.0276 StartY=15.4549 StartZ=0 EndX=18.6312 EndY=3.16764 EndZ=0
    g2: LineSegment StartX=18.6312 StartY=3.16764 StartZ=0 EndX=17.8121 EndY=2.59406 EndZ=0
    g3: LineSegment StartX=17.8121 StartY=2.59406 StartZ=0 EndX=9.20845 EndY=14.8813 EndZ=0
  constraints (12):
    c: Coincident(g0,g1)
    c: Coincident(g1,g2)
    c: Coincident(g2,g3)
    c: Coincident(g3,g0)
    c: Perpendicular(g1,g2)
    c: Perpendicular(g2,g3)
    c: Perpendicular(g1,g0)
    c: Distance(g1) = 15  'width'
    c: Distance(g2) = 1
    c: Distance(g-1,g0) = 17.5  'top_corner_distance'
    c: Distance(g-1,g2) = 18  'bottom_corner_distance'
    c: Angle(g3) = 2.18166  'angle'
FEATURE [PartDesign::ShapeBinder] ShapeBinder002
  Placement = pos=(9.65,-7,8.75) rot=(0.707107,0,-0.707107;3.14159rad)
  Support = -> [COMPOUND176_copy_mp_cp001]
  TraceSupport = false
FEATURE [PartDesign::ShapeBinder] ShapeBinder003  label="Heatsink_ShapeBinder"
  Placement = pos=(11.4,-16.58,-7.25) rot=(0.707107,0,0.707107;3.14159rad)
  Support = -> [Body004002]
  TraceSupport = false
FEATURE [Sketcher::SketchObject] Sketch015  label="pos_test_Sketch"
  AttachmentOffset = pos=(0,0,12) rot=(0,0,1;0rad)
  ExternalGeometry = -> [ShapeBinder002,ShapeBinder003]
  MapMode = 5
  Placement = pos=(0,0,12) rot=(0,0,1;0rad)
  Support = -> [XY_Plane039]
  sketch-geometry (3):
    g0: LineSegment StartX=9.14 StartY=-7 StartZ=0 EndX=25.14 EndY=-7 EndZ=0
    g1: LineSegment StartX=15.2 StartY=-6.24667 StartZ=0 EndX=15.2 EndY=-7.74667 EndZ=0
    g2: GeomPoint X=15.2 Y=-6.99667 Z=0
  constraints (6):
    c: Horizontal(g0)
    c: Symmetric(g-3,g-3,g0)
    c: DistanceX(g0,g0) = 16
    c: Coincident(g1,g-4)
    c: Coincident(g1,g-5)
    c: Symmetric(g1,g1,g2)
FEATURE [Sketcher::SketchObject] Sketch016  label="heatsink_pos_helper_XY_Sketch"
  AttachmentOffset = pos=(0,0,12) rot=(0,0,1;0rad)
  ExternalGeometry = -> [ShapeBinder002,ShapeBinder003]
  MapMode = 5
  Placement = pos=(0,0,12) rot=(0,0,1;0rad)
  Support = -> [XY_Plane039]
  sketch-geometry (4):
    g0: LineSegment [constr] StartX=9.14 StartY=-7 StartZ=0 EndX=25.14 EndY=-7 EndZ=0
    g1: LineSegment [constr] StartX=15.2 StartY=-6.24667 StartZ=0 EndX=15.2 EndY=-7.74667 EndZ=0
    g2: GeomPoint X=15.2 Y=-6.99667 Z=0
    g3: LineSegment StartX=15.2 StartY=1.42 StartZ=0 EndX=15.2 EndY=-7.74667 EndZ=0
  constraints (10):
    c: Horizontal(g0)
    c: Symmetric(g-3,g-3,g0)
    c: DistanceX(g0,g0) = 16
    c: Coincident(g1,g-4)
    c: Coincident(g1,g-5)
    c: Symmetric(g1,g1,g2)
    c: Vertical(g3)
    c: Coincident(g3,g1)
    c: PointOnObject(g3,g-6)
    c: DistanceY(g3,g3) = 9.16667
FEATURE [PartDesign::ShapeBinder] ShapeBinder004
  Placement = pos=(0,0,12) rot=(0,0,1;0rad)
  Support = -> [Sketch016]
  TraceSupport = false
FEATURE [PartDesign::ShapeBinder] ShapeBinder005
  Placement = pos=(9.65,-7,8.75) rot=(0.707107,0,-0.707107;3.14159rad)
  Support = -> [COMPOUND176_copy_mp_cp001]
  TraceSupport = false
FEATURE [Sketcher::SketchObject] Sketch017  label="heatsink_pos_helper_Z_Sketch"
  AttachmentOffset = pos=(0,0,10) rot=(0,0,1;0rad)
  ExternalGeometry = -> [ShapeBinder005,ShapeBinder003]
  MapMode = 5
  Placement = pos=(0,-10,-2.2e-15) rot=(1,0,0;1.5708rad)
  Support = -> [XZ_Plane039]
  sketch-geometry (2):
    g0: LineSegment StartX=9.14 StartY=8.75 StartZ=0 EndX=14.7 EndY=8.75 EndZ=0
    g1: GeomPoint X=14.7 Y=7.87 Z=0
  constraints (8):
    c: Horizontal(g0)
    c: Symmetric(g-3,g-3,g0)
    c: PointOnObject(g0,g-4)
    c: DistanceY(g-4,g-4) = 1.8
    c: Symmetric(g-4,g-4,g1)
    c: DistanceY(g1,g0) = 0.88
    c: DistanceY(g-4,g-5) = 1.98
    c: DistanceY(g-6,g-4) = 1.98
FEATURE [Sketcher::SketchObject] Sketch018  label="mounting_screw_holes_Sketch"
  AttachmentOffset = pos=(0,0,8) rot=(0,0,1;0rad)
  MapMode = 5
  Placement = pos=(0,0,8) rot=(0,0,1;0rad)
  Support = -> [XY_Plane023]
  expr: Constraints[6] = (5.5 + 0.5) / 2
  sketch-geometry (16):
    g0: LineSegment [constr] StartX=-17.9562 StartY=1.25562 StartZ=0 EndX=17.9562 EndY=-1.25562 EndZ=0
    g1: LineSegment [constr] StartX=-1.25562 StartY=-17.9562 StartZ=0 EndX=1.25562 EndY=17.9562 EndZ=0
    g2: Circle CenterX=1.25562 CenterY=17.9562 CenterZ=0 NormalX=0 NormalY=0 NormalZ=1 AngleXU=0 Radius=3
    g3: Circle [constr] CenterX=1.25562 CenterY=17.9562 CenterZ=0 NormalX=0 NormalY=0 NormalZ=1 AngleXU=0 Radius=1.25
    g4: Circle [constr] CenterX=1.25562 CenterY=17.9562 CenterZ=0 NormalX=0 NormalY=0 NormalZ=1 AngleXU=0 Radius=4
    g5: Circle [constr] CenterX=17.9562 CenterY=-1.25562 CenterZ=0 NormalX=0 NormalY=0 NormalZ=1 AngleXU=0 Radius=1.25
    g6: Circle CenterX=-1.25562 CenterY=-17.9562 CenterZ=0 NormalX=0 NormalY=0 NormalZ=1 AngleXU=0 Radius=3
    g7: Circle CenterX=-17.9562 CenterY=1.25562 CenterZ=0 NormalX=0 NormalY=0 NormalZ=1 AngleXU=0 Radius=3
    g8: Circle CenterX=17.9562 CenterY=-1.25562 CenterZ=0 NormalX=0 NormalY=0 NormalZ=1 AngleXU=0 Radius=3
    g9: LineSegment [constr] StartX=-16.3684 StartY=-1.49438 StartZ=0 EndX=-14.7807 EndY=1.25562 EndZ=0
    g10: LineSegment [constr] StartX=-14.7807 StartY=1.25562 StartZ=0 EndX=-16.3684 EndY=4.00562 EndZ=0
    g11: LineSegment [constr] StartX=-16.3684 StartY=4.00562 StartZ=0 EndX=-19.5439 EndY=4.00562 EndZ=0
    g12: LineSegment [constr] StartX=-19.5439 StartY=4.00562 StartZ=0 EndX=-21.1316 EndY=1.25562 EndZ=0
    g13: LineSegment [constr] StartX=-21.1316 StartY=1.25562 StartZ=0 EndX=-19.5439 EndY=-1.49438 EndZ=0
    g14: LineSegment [constr] StartX=-19.5439 StartY=-1.49438 StartZ=0 EndX=-16.3684 EndY=-1.49438 EndZ=0
    g15: Circle [constr] CenterX=-17.9562 CenterY=1.25562 CenterZ=0 NormalX=0 NormalY=0 NormalZ=1 AngleXU=0 Radius=3.17543
  constraints (36):
    c: Symmetric(g1,g1,g-1)
    c: Symmetric(g0,g0,g-1)
    c: Perpendicular(g1,g0)
    c: Angle(g1,g-1) = 1.64061
    c: Equal(g0,g1)
    c: Coincident(g2,g1)
    c: Radius(g2) = 3
    c: Distance(g-1,g2) = 18
    c: Diameter(g3) = 2.5
    c: Coincident(g3,g2)
    c: Coincident(g4,g2)
    c: Diameter(g4) = 8
    c: Coincident(g5,g0)
    c: Equal(g5,g3)
    c: Coincident(g6,g1)
    c: Equal(g2,g6)
    c: Coincident(g7,g0)
    c: Equal(g2,g7)
    c: Equal(g7,g8)
    c: Coincident(g8,g0)
    c: Coincident(g9,g10)
    c: Coincident(g10,g11)
    c: Coincident(g11,g12)
    c: Coincident(g12,g13)
    c: Coincident(g13,g14)
    c: Coincident(g14,g9)
    c: Equal(g9, g10-g14) x5
    c: PointOnObject(g9,g15)
    c: PointOnObject(g10,g15)
    c: PointOnObject(g11,g15)
    c: PointOnObject(g12,g15)
    c: PointOnObject(g13,g15)
    c: PointOnObject(g14,g15)
    c: Coincident(g15,g7)
    c: Distance(g10,g9) = 5.5
    c: Horizontal(g14)
FEATURE [PartDesign::Pad] Pad008
  Length = 22
  Length2 = 100
  Profile = -> Sketch014
  Reversed = true
  Type = 0
  expr: Length = data.lightblocker_side_height / 2
FEATURE [Sketcher::SketchObject] Sketch021  label="lightblocker_side_slot_Sketch"
  MapMode = 5
  Support = -> [XY_Plane023]
  expr: Constraints[24] = lightblocker_side_profile_Sketch.Constraints.angle
  expr: Constraints[23] = lightblocker_side_profile_Sketch.Constraints.bottom_corner_distance
  expr: Constraints[22] = lightblocker_side_profile_Sketch.Constraints.top_corner_distance
  expr: Constraints[21] = data.wood2_thickness
  expr: Constraints[12] = lightblocker_side_profile_Sketch.Constraints.width
  sketch-geometry (9):
    g0: LineSegment [constr] StartX=9.20845 StartY=14.8813 StartZ=0 EndX=10.0276 EndY=15.4549 EndZ=0
    g1: LineSegment [constr] StartX=10.0276 StartY=15.4549 StartZ=0 EndX=18.6312 EndY=3.16764 EndZ=0
    g2: LineSegment [constr] StartX=18.6312 StartY=3.16764 StartZ=0 EndX=17.8121 EndY=2.59406 EndZ=0
    g3: LineSegment StartX=11.216 StartY=12.0143 StartZ=0 EndX=12.0351 EndY=12.5879 EndZ=0
    g4: LineSegment StartX=12.0351 StartY=12.5879 StartZ=0 EndX=16.6237 EndY=6.03467 EndZ=0
    g5: LineSegment StartX=16.6237 StartY=6.03467 StartZ=0 EndX=15.8046 EndY=5.4611 EndZ=0
    g6: LineSegment StartX=15.8046 StartY=5.4611 StartZ=0 EndX=11.216 EndY=12.0143 EndZ=0
    g7: LineSegment [constr] StartX=9.20845 StartY=14.8813 StartZ=0 EndX=11.216 EndY=12.0143 EndZ=0
    g8: LineSegment [constr] StartX=15.8046 StartY=5.4611 StartZ=0 EndX=17.8121 EndY=2.59406 EndZ=0
  constraints (26):
    c: Coincident(g0,g1)
    c: Coincident(g1,g2)
    c: Coincident(g3,g4)
    c: Coincident(g4,g5)
    c: Coincident(g5,g6)
    c: Coincident(g6,g3)
    c: PointOnObject(g4,g1)
    c: Perpendicular(g1,g2)
    c: Perpendicular(g1,g0)
    c: PointOnObject(g3,g1)
    c: Perpendicular(g4,g5)
    c: Perpendicular(g4,g3)
    c: Distance(g1) = 15
    c: Coincident(g7,g0)
    c: Coincident(g7,g3)
    c: Coincident(g8,g5)
    c: Coincident(g8,g2)
    c: Equal(g8,g7)
    c: Perpendicular(g2,g8)
    c: Perpendicular(g3,g6)
    c: Perpendicular(g0,g7)
    c: Distance(g2) = 1
    c: Distance(g-1,g0) = 17.5
    c: Distance(g-1,g2) = 18
    c: Angle(g6) = 2.18166
    c: Distance(g4) = 8
FEATURE [Sketcher::SketchObject] Sketch022  label="heatsink_cutout_helper_Sketch"
  ExternalGeometry = -> [ShapeBinder003]
  MapMode = 5
  Placement = pos=(13.9901,9.79595,0) rot=(0.345437,0.663579,0.663579;2.47638rad)
  Support = -> [Pad008]
  sketch-geometry (18):
    g0: LineSegment StartX=-15.1641 StartY=10.75 StartZ=0 EndX=-5.37558 EndY=10.75 EndZ=0
    g1: LineSegment StartX=-5.37558 StartY=10.75 StartZ=0 EndX=-5.37558 EndY=8.67 EndZ=0
    g2: LineSegment StartX=-5.37558 StartY=8.67 StartZ=0 EndX=-15.1641 EndY=8.67 EndZ=0
    g3: LineSegment StartX=-15.1641 StartY=8.67 StartZ=0 EndX=-15.1641 EndY=10.75 EndZ=0
    g4: LineSegment StartX=-16.4628 StartY=7.07 StartZ=0 EndX=-3.46283 EndY=7.07 EndZ=0
    g5: LineSegment StartX=-3.46283 StartY=7.07 StartZ=0 EndX=-3.46283 EndY=-21.57 EndZ=0
    g6: LineSegment StartX=-3.46283 StartY=-21.57 StartZ=0 EndX=-16.4628 EndY=-21.57 EndZ=0
    g7: LineSegment StartX=-16.4628 StartY=-21.57 StartZ=0 EndX=-16.4628 EndY=7.07 EndZ=0
    g8: LineSegment StartX=-15.1641 StartY=-23.17 StartZ=0 EndX=-5.37558 EndY=-23.17 EndZ=0
    g9: LineSegment StartX=-5.37558 StartY=-23.17 StartZ=0 EndX=-5.37558 EndY=-25.25 EndZ=0
    g10: LineSegment StartX=-5.37558 StartY=-25.25 StartZ=0 EndX=-15.1641 EndY=-25.25 EndZ=0
    g11: LineSegment StartX=-15.1641 StartY=-25.25 StartZ=0 EndX=-15.1641 EndY=-23.17 EndZ=0
    g12: LineSegment [constr] StartX=-15.1641 StartY=8.67 StartZ=0 EndX=-15.1641 EndY=7.07 EndZ=0
    g13: LineSegment [constr] StartX=-15.1641 StartY=-23.17 StartZ=0 EndX=-15.1641 EndY=-21.57 EndZ=0
    g14: LineSegment [constr] StartX=-9.96283 StartY=-21.57 StartZ=0 EndX=-9.96283 EndY=-25.25 EndZ=0
    g15: LineSegment [constr] StartX=-14.5501 StartY=-25.25 StartZ=0 EndX=-5.37558 EndY=-25.25 EndZ=0
    g16: LineSegment [constr] StartX=-14.5501 StartY=10.75 StartZ=0 EndX=-5.37558 EndY=10.75 EndZ=0
    g17: LineSegment [constr] StartX=-15.0641 StartY=8.67 StartZ=0 EndX=-15.0641 EndY=10.75 EndZ=0
  constraints (53):
    c: Coincident(g0,g1)
    c: Coincident(g1,g2)
    c: Coincident(g2,g3)
    c: Coincident(g3,g0)
    c: Horizontal(g0)
    c: Horizontal(g2)
    c: Vertical(g1)
    c: Vertical(g3)
    c: Coincident(g4,g5)
    c: Coincident(g5,g6)
    c: Coincident(g6,g7)
    c: Coincident(g7,g4)
    c: Horizontal(g4)
    c: Horizontal(g6)
    c: Vertical(g5)
    c: Vertical(g7)
    c: Coincident(g8,g9)
    c: Coincident(g9,g10)
    c: Coincident(g11,g8)
    c: Horizontal(g8)
    c: Vertical(g9)
    c: Vertical(g11)
    c: Equal(g1,g9)
    c: Equal(g0,g8)
    c: DistanceX(g6,g6) = 13
    c: DistanceY(g9,g0) = 36
    c: PointOnObject(g12,g4)
    c: Vertical(g12)
    c: Coincident(g13,g8)
    c: PointOnObject(g13,g6)
    c: Vertical(g13)
    c: Equal(g13,g12)
    c: Coincident(g12,g2)
    c: PointOnObject(g8,g1)
    c: Vertical(g14)
    c: Symmetric(g6,g6,g14)
    c: Coincident(g10,g11)
    c: DistanceY(g8,g13) = 1.6
    c: Horizontal(g15)
    c: Coincident(g15,g9)
    c: Equal(g11,g3)
    c: Horizontal(g16)
    c: Coincident(g0,g16)
    c: Equal(g16,g15)
    c: Symmetric(g15,g15,g14)
    c: PointOnObject(g16,g-3)
    c: DistanceY(g-3,g16) = 0
    c: PointOnObject(g0,g-4)
    c: DistanceX(g0,g-5) = 0.1
    c: Coincident(g17,g-5)
    c: Vertical(g17)
    c: DistanceY(g17,g-5) = 0.1
    c: Equal(g17,g3)
FEATURE [PartDesign::Body] Body004019  label="LEDBoard_Heatsink_position_helper_Body"
  Group = -> [Sketch015,ShapeBinder002,ShapeBinder003,Sketch016,Sketch017,ShapeBinder005,Sketch022]
  Origin = -> Origin039
FEATURE [App::Part] Part002  label="LEDBoards_Part"
  Group = -> [COMPOUND176_copy_mp_cp002,COMPOUND176_copy_mp_cp003,COMPOUND176_copy_mp_cp004,COMPOUND176_copy_mp_cp001,Body004002,Body004003,Body004004,Body004005,Body004019]
  Origin = -> Origin006
  Placement = pos=(0,0,-15.25) rot=(0,0,1;0rad)
FEATURE [Sketcher::SketchObject] Sketch023  label="heatsink_cutout_helper_Sketch001"
  ExternalGeometry = -> [ShapeBinder003]
  MapMode = 5
  Placement = pos=(13.9901,9.79595,0) rot=(0.345437,0.663579,0.663579;2.47638rad)
  Support = -> [Pad008]
  sketch-geometry (18):
    g0: LineSegment StartX=-15.1641 StartY=-4.5 StartZ=0 EndX=-5.37558 EndY=-4.5 EndZ=0
    g1: LineSegment StartX=-5.37558 StartY=-4.5 StartZ=0 EndX=-5.37558 EndY=-6.58 EndZ=0
    g2: LineSegment StartX=-5.37558 StartY=-6.58 StartZ=0 EndX=-15.1641 EndY=-6.58 EndZ=0
    g3: LineSegment StartX=-15.1641 StartY=-6.58 StartZ=0 EndX=-15.1641 EndY=-4.5 EndZ=0
    g4: LineSegment StartX=-16.4628 StartY=-8.18 StartZ=0 EndX=-3.46283 EndY=-8.18 EndZ=0
    g5: LineSegment StartX=-3.46283 StartY=-8.18 StartZ=0 EndX=-3.46283 EndY=-36.82 EndZ=0
    g6: LineSegment StartX=-3.46283 StartY=-36.82 StartZ=0 EndX=-16.4628 EndY=-36.82 EndZ=0
    g7: LineSegment StartX=-16.4628 StartY=-36.82 StartZ=0 EndX=-16.4628 EndY=-8.18 EndZ=0
    g8: LineSegment StartX=-15.1641 StartY=-38.42 StartZ=0 EndX=-5.37558 EndY=-38.42 EndZ=0
    g9: LineSegment StartX=-5.37558 StartY=-38.42 StartZ=0 EndX=-5.37558 EndY=-40.5 EndZ=0
    g10: LineSegment StartX=-5.37558 StartY=-40.5 StartZ=0 EndX=-15.1641 EndY=-40.5 EndZ=0
    g11: LineSegment StartX=-15.1641 StartY=-40.5 StartZ=0 EndX=-15.1641 EndY=-38.42 EndZ=0
    g12: LineSegment [constr] StartX=-15.1641 StartY=-6.58 StartZ=0 EndX=-15.1641 EndY=-8.18 EndZ=0
    g13: LineSegment [constr] StartX=-15.1641 StartY=-38.42 StartZ=0 EndX=-15.1641 EndY=-36.82 EndZ=0
    g14: LineSegment [constr] StartX=-9.96283 StartY=-36.82 StartZ=0 EndX=-9.96283 EndY=-40.5 EndZ=0
    g15: LineSegment [constr] StartX=-14.5501 StartY=-40.5 StartZ=0 EndX=-5.37558 EndY=-40.5 EndZ=0
    g16: LineSegment [constr] StartX=-14.5501 StartY=-4.5 StartZ=0 EndX=-5.37558 EndY=-4.5 EndZ=0
    g17: LineSegment [constr] StartX=-15.0641 StartY=8.67 StartZ=0 EndX=-15.0641 EndY=10.75 EndZ=0
  constraints (53):
    c: Coincident(g0,g1)
    c: Coincident(g1,g2)
    c: Coincident(g2,g3)
    c: Coincident(g3,g0)
    c: Horizontal(g0)
    c: Horizontal(g2)
    c: Vertical(g1)
    c: Vertical(g3)
    c: Coincident(g4,g5)
    c: Coincident(g5,g6)
    c: Coincident(g6,g7)
    c: Coincident(g7,g4)
    c: Horizontal(g4)
    c: Horizontal(g6)
    c: Vertical(g5)
    c: Vertical(g7)
    c: Coincident(g8,g9)
    c: Coincident(g9,g10)
    c: Coincident(g11,g8)
    c: Horizontal(g8)
    c: Vertical(g9)
    c: Vertical(g11)
    c: Equal(g1,g9)
    c: Equal(g0,g8)
    c: DistanceX(g6,g6) = 13
    c: DistanceY(g9,g0) = 36
    c: PointOnObject(g12,g4)
    c: Vertical(g12)
    c: Coincident(g13,g8)
    c: PointOnObject(g13,g6)
    c: Vertical(g13)
    c: Equal(g13,g12)
    c: Coincident(g12,g2)
    c: PointOnObject(g8,g1)
    c: Vertical(g14)
    c: Symmetric(g6,g6,g14)
    c: Coincident(g10,g11)
    c: DistanceY(g8,g13) = 1.6
    c: Horizontal(g15)
    c: Coincident(g15,g9)
    c: Equal(g11,g3)
    c: Horizontal(g16)
    c: Coincident(g0,g16)
    c: Equal(g16,g15)
    c: Symmetric(g15,g15,g14)
    c: PointOnObject(g16,g-3)
    c: DistanceY(g-3,g16) = -15.25
    c: PointOnObject(g0,g-4)
    c: DistanceX(g0,g-5) = 0.1
    c: Coincident(g17,g-5)
    c: Vertical(g17)
    c: DistanceY(g17,g-5) = 0.1
    c: Equal(g17,g3)
FEATURE [PartDesign::Pad] Pad009
  Length = 4
  Length2 = 100
  Profile = -> Sketch
  Reversed = true
  Type = 0
  expr: Length = data.wood_thickness
FEATURE [Sketcher::SketchObject] Sketch024
  MapMode = 5
  Support = -> [XY_Plane044]
  sketch-geometry (4):
    g0: LineSegment StartX=-10 StartY=10 StartZ=0 EndX=10 EndY=10 EndZ=0
    g1: LineSegment StartX=10 StartY=10 StartZ=0 EndX=10 EndY=-10 EndZ=0
    g2: LineSegment StartX=10 StartY=-10 StartZ=0 EndX=-10 EndY=-10 EndZ=0
    g3: LineSegment StartX=-10 StartY=-10 StartZ=0 EndX=-10 EndY=10 EndZ=0
  constraints (11):
    c: Coincident(g0,g1)
    c: Coincident(g1,g2)
    c: Coincident(g2,g3)
    c: Coincident(g3,g0)
    c: Horizontal(g0)
    c: Horizontal(g2)
    c: Vertical(g1)
    c: Vertical(g3)
    c: Symmetric(g2,g0,g-1)
    c: Equal(g0,g1)
    c: DistanceY(g1,g1) = 20
FEATURE [TechDraw::DrawSVGTemplate] Template002 .. Template006  x5 (patterned run collapsed; names and placements below)
  Height = 210
  Orientation = 1
  Width = 297
FEATURE [PartDesign::FeatureBase] Clone019
  BaseFeature = -> Body001001
FEATURE [PartDesign::Body] Body004025  label="crystal_Body_SimpleCopy_clone2"
  BaseFeature = -> Body001001
  Group = -> [Clone019]
  Origin = -> Origin045
  Placement = pos=(0,0,-5) rot=(0,0,1;0rad)
  Tip = -> Clone019
  expr: Placement.Base.z = data.crystal_mounting_fit_offset - 4
FEATURE [PartDesign::FeatureBase] Clone020
  BaseFeature = -> Body001001
FEATURE [PartDesign::Body] Body004026  label="crystal_Body_SimpleCopy_clone1"
  BaseFeature = -> Body001001
  Group = -> [Clone020]
  Origin = -> Origin046
  Placement = pos=(0,0,-1) rot=(0,0,1;0rad)
  Tip = -> Clone020
  expr: Placement.Base.z = data.crystal_mounting_fit_offset
FEATURE [TechDraw::DrawSVGTemplate] Template007
  EditableTexts = Designed_by_Name=Stefan Krüger,FC-Date=24.03.2019 10:00,FC-SC=1:1,FC-SH=1/1,FC-Title=Magic Crystal,Subtitle=a magically sparkling crystal,+3 more (map truncated)
  Height = 210
  Orientation = 1
  Width = 297
FEATURE [Sketcher::SketchObject] Sketch025
  MapMode = 5
  Support = -> [XY_Plane047]
  sketch-geometry (7):
    g0: LineSegment StartX=-2.75 StartY=-1.58771 StartZ=0 EndX=-4e-16 EndY=-3.17543 EndZ=0
    g1: LineSegment StartX=-4e-16 StartY=-3.17543 StartZ=0 EndX=2.75 EndY=-1.58771 EndZ=0
    g2: LineSegment StartX=2.75 StartY=-1.58771 StartZ=0 EndX=2.75 EndY=1.58771 EndZ=0
    g3: LineSegment StartX=2.75 StartY=1.58771 StartZ=0 EndX=4e-16 EndY=3.17543 EndZ=0
    g4: LineSegment StartX=4e-16 StartY=3.17543 StartZ=0 EndX=-2.75 EndY=1.58771 EndZ=0
    g5: LineSegment StartX=-2.75 StartY=1.58771 StartZ=0 EndX=-2.75 EndY=-1.58771 EndZ=0
    g6: Circle [constr] CenterX=0 CenterY=0 CenterZ=0 NormalX=0 NormalY=0 NormalZ=1 AngleXU=0 Radius=3.17543
  constraints (16):
    c: Coincident(g0,g1)
    c: Coincident(g1,g2)
    c: Coincident(g2,g3)
    c: Coincident(g3,g4)
    c: Coincident(g4,g5)
    c: Coincident(g5,g0)
    c: Equal(g0, g1-g5) x5
    c: PointOnObject(g0,g6)
    c: PointOnObject(g1,g6)
    c: PointOnObject(g2,g6)
    c: PointOnObject(g3,g6)
    c: PointOnObject(g4,g6)
    c: PointOnObject(g5,g6)
    c: Coincident(g6,g-1)
    c: Distance(g4,g0) = 5.5
    c: Vertical(g2)
FEATURE [PartDesign::Pad] Pad010
  Length = 2.4
  Length2 = 100
  Profile = -> Sketch025
  Reversed = true
  Type = 0
FEATURE [Sketcher::SketchObject] Sketch026
  MapMode = 5
  Support = -> [XY_Plane047]
  sketch-geometry (1):
    g0: Circle CenterX=0 CenterY=0 CenterZ=0 NormalX=0 NormalY=0 NormalZ=1 AngleXU=0 Radius=3
  constraints (2):
    c: Coincident(g0,g-1)
    c: Radius(g0) = 3
FEATURE [PartDesign::Hole] Hole004
  BaseFeature = -> Pad010
  Depth = 25
  DepthType = 1
  Diameter = 2.5
  DrillPoint = 1
  DrillPointAngle = 118
  HoleCutCountersinkAngle = 90
  HoleCutDepth = 0
  HoleCutDiameter = 3
  HoleCutType = 0
  ModelActualThread = false
  Profile = -> Sketch026
  Tapered = false
  TaperedAngle = 90
  ThreadAngle = 60
  ThreadClass = 0
  ThreadCutOffInner = 0.0541266
  ThreadCutOffOuter = 0.108253
  ThreadDirection = 1
  ThreadFit = 0
  ThreadPitch = 0.5
  ThreadSize = 3
  ThreadType = 1
  Threaded = true
FEATURE [PartDesign::Body] Body004027  label="M3_Nut_Body"
  Group = -> [Sketch025,Pad010,Sketch026,Hole004]
  Origin = -> Origin047
  Tip = -> Hole004
FEATURE [PartDesign::FeatureBase] Clone021
  BaseFeature = -> Body004027
FEATURE [PartDesign::Body] Body004028  label="M3_Nut_Clone"
  BaseFeature = -> Body004027
  Group = -> [Clone021]
  Origin = -> Origin048
  Placement = pos=(17.7,-1.25,-6.5) rot=(0,0,1;0rad)
  Tip = -> Clone021
FEATURE [PartDesign::FeatureBase] Clone022
  BaseFeature = -> Body004027
FEATURE [PartDesign::Body] Body004029  label="M3_Nut_Clone2"
  BaseFeature = -> Body004027
  Group = -> [Clone022]
  Origin = -> Origin049
  Placement = pos=(17.8,-1.25,-36) rot=(0,0,1;0rad)
  Tip = -> Clone022
FEATURE [Sketcher::SketchObject] Sketch027  label="lightblocker_side_slot_cutaway_Sketch"
  MapMode = 5
  Support = -> [XY_Plane023]
  expr: Constraints[19] = lightblocker_side_profile_Sketch.Constraints.width
  expr: Constraints[17] = lightblocker_side_profile_Sketch.Constraints.angle
  expr: Constraints[14] = data.wood2_thickness
  expr: Constraints[16] = lightblocker_side_profile_Sketch.Constraints.bottom_corner_distance
  expr: Constraints[15] = lightblocker_side_profile_Sketch.Constraints.top_corner_distance
  sketch-geometry (10):
    g0: LineSegment StartX=9.20845 StartY=14.8813 StartZ=0 EndX=10.0276 EndY=15.4549 EndZ=0
    g1: LineSegment StartX=18.6312 StartY=3.16764 StartZ=0 EndX=17.8121 EndY=2.59406 EndZ=0
    g2: LineSegment StartX=11.216 StartY=12.0143 StartZ=0 EndX=12.0351 EndY=12.5879 EndZ=0
    g3: LineSegment [constr] StartX=12.0351 StartY=12.5879 StartZ=0 EndX=16.6237 EndY=6.03467 EndZ=0
    g4: LineSegment StartX=16.6237 StartY=6.03467 StartZ=0 EndX=15.8046 EndY=5.4611 EndZ=0
    g5: LineSegment [constr] StartX=15.8046 StartY=5.4611 StartZ=0 EndX=11.216 EndY=12.0143 EndZ=0
    g6: LineSegment StartX=9.20845 StartY=14.8813 StartZ=0 EndX=11.216 EndY=12.0143 EndZ=0
    g7: LineSegment StartX=15.8046 StartY=5.4611 StartZ=0 EndX=17.8121 EndY=2.59406 EndZ=0
    g8: LineSegment StartX=18.6312 StartY=3.16764 StartZ=0 EndX=16.6237 EndY=6.03467 EndZ=0
    g9: LineSegment StartX=10.0276 StartY=15.4549 StartZ=0 EndX=12.0351 EndY=12.5879 EndZ=0
  constraints (28):
    c: Coincident(g2,g3)
    c: Coincident(g3,g4)
    c: Coincident(g4,g5)
    c: Coincident(g5,g2)
    c: Perpendicular(g3,g4)
    c: Perpendicular(g3,g2)
    c: Coincident(g6,g0)
    c: Coincident(g6,g2)
    c: Coincident(g7,g4)
    c: Coincident(g7,g1)
    c: Equal(g7,g6)
    c: Perpendicular(g1,g7)
    c: Perpendicular(g2,g5)
    c: Perpendicular(g0,g6)
    c: Distance(g1) = 1
    c: Distance(g-1,g0) = 17.5
    c: Distance(g-1,g1) = 18
    c: Angle(g5) = 2.18166
    c: Distance(g3) = 8
    c: Distance(g1,g0) = 15
    c: Coincident(g8,g1)
    c: Coincident(g8,g3)
    c: Perpendicular(g1,g8)
    c: Coincident(g9,g0)
    c: Coincident(g9,g2)
    c: Parallel(g8,g3)
    c: Parallel(g3,g9)
    c: Parallel(g6,g9)
FEATURE [PartDesign::Mirrored] Mirrored
  BaseFeature = -> Pad008
  MirrorPlane = -> Pad008 [Face6]
  Originals = -> [Pad008]
FEATURE [PartDesign::Pocket] Pocket008
  BaseFeature = -> Mirrored
  Length = 4
  Length2 = 100
  Profile = -> Sketch027
  Type = 0
  expr: Length = data.wood_thickness
FEATURE [PartDesign::Mirrored] Mirrored001
  BaseFeature = -> Pocket008
  MirrorPlane = -> Pad008 [Face6]
  Originals = -> [Pocket008]
  Refine = true
FEATURE [PartDesign::Body] Body004020  label="lightblocker_side_Body"
  Group = -> [Pad008,Sketch023,Mirrored,Pocket008,Mirrored001]
  Origin = -> Origin040
  Tip = -> Mirrored001
FEATURE [PartDesign::FeatureBase] Clone016
  BaseFeature = -> Body004020
FEATURE [PartDesign::Body] Body004021  label="lightblocker_side_Clone2"
  BaseFeature = -> Body004020
  Group = -> [Clone016]
  Origin = -> Origin041
  Placement = pos=(0,0,0) rot=(0,0,-1;1.5708rad)
  Tip = -> Clone016
FEATURE [PartDesign::FeatureBase] Clone017
  BaseFeature = -> Body004020
FEATURE [PartDesign::Body] Body004022  label="lightblocker_side_Clone3"
  BaseFeature = -> Body004020
  Group = -> [Clone017]
  Origin = -> Origin042
  Placement = pos=(0,0,0) rot=(0,0,1;3.14159rad)
  Tip = -> Clone017
FEATURE [PartDesign::FeatureBase] Clone018
  BaseFeature = -> Body004020
FEATURE [PartDesign::Body] Body004023  label="lightblocker_side_Clone4"
  BaseFeature = -> Body004020
  Group = -> [Clone018]
  Origin = -> Origin043
  Placement = pos=(0,0,0) rot=(0,0,1;1.5708rad)
  Tip = -> Clone018
FEATURE [PartDesign::PolarPattern] PolarPattern002
  Angle = 360
  Axis = -> Sketch [N_Axis]
  BaseFeature = -> Pad006
  Occurrences = 4
  Originals = -> [Pad006]
FEATURE [PartDesign::Pocket] Pocket001
  BaseFeature = -> PolarPattern002
  Length = 5
  Length2 = 100
  Profile = -> Sketch012
  Type = 1
FEATURE [PartDesign::Hole] Hole
  BaseFeature = -> Pocket001
  Depth = 25
  DepthType = 1
  Diameter = 3.3
  DrillPoint = 1
  DrillPointAngle = 118
  HoleCutCountersinkAngle = 90
  HoleCutDepth = 0
  HoleCutDiameter = 3
  HoleCutType = 0
  ModelActualThread = false
  Profile = -> Sketch018
  Tapered = false
  TaperedAngle = 90
  ThreadAngle = 0
  ThreadClass = 0
  ThreadCutOffInner = 0
  ThreadCutOffOuter = 0
  ThreadDirection = 0
  ThreadFit = 0
  ThreadPitch = 0
  ThreadSize = 3
  ThreadType = 1
  Threaded = false
FEATURE [PartDesign::Pocket] Pocket005
  BaseFeature = -> Hole
  Length = 5
  Length2 = 100
  Profile = -> Sketch021
  Type = 1
FEATURE [PartDesign::PolarPattern] PolarPattern
  Angle = 360
  Axis = -> Sketch021 [N_Axis]
  BaseFeature = -> Pocket005
  Occurrences = 4
  Originals = -> [Pocket005]
  Refine = true
FEATURE [PartDesign::Body] Body004008  label="lightguides_mounting_Body"
  Group = -> [Pad006,PolarPattern002,Pocket001,Hole,Pocket005,PolarPattern]
  Origin = -> Origin024
  Tip = -> PolarPattern
FEATURE [TechDraw::DrawViewPart] View004
  CoarseView = false
  Direction = (0,0,1)
  Focus = 100
  HardHidden = false
  IsoCount = 0
  IsoHidden = false
  IsoVisible = false
  LockPosition = false
  Perspective = false
  Rotation = 0
  ScaleType = 0
  SeamHidden = false
  SeamVisible = false
  SmoothHidden = false
  SmoothVisible = false
  Source = -> [Body004008]
  X = 148.5
  Y = 105
FEATURE [TechDraw::DrawPage] Page004  label="lightguides_mounting_Page"
  KeepUpdated = true
  ProjectionType = 0
  Template = -> Template004
  Views = -> [View004]
FEATURE [PartDesign::PolarPattern] PolarPattern003
  Angle = 360
  Axis = -> Sketch [N_Axis]
  BaseFeature = -> Pad009
  Occurrences = 4
  Originals = -> [Pad009]
FEATURE [PartDesign::Hole] Hole003
  BaseFeature = -> PolarPattern003
  Depth = 25
  DepthType = 0
  Diameter = 3.3
  DrillPoint = 1
  DrillPointAngle = 118
  HoleCutCountersinkAngle = 90
  HoleCutDepth = 0
  HoleCutDiameter = 3
  HoleCutType = 0
  ModelActualThread = false
  Profile = -> Sketch018
  Tapered = false
  TaperedAngle = 90
  ThreadAngle = 0
  ThreadClass = 0
  ThreadCutOffInner = 0
  ThreadCutOffOuter = 0
  ThreadDirection = 0
  ThreadFit = 0
  ThreadPitch = 0
  ThreadSize = 3
  ThreadType = 1
  Threaded = false
FEATURE [PartDesign::Pocket] Pocket006
  BaseFeature = -> Hole003
  Length = 5
  Length2 = 100
  Profile = -> Sketch021
  Type = 1
FEATURE [PartDesign::PolarPattern] PolarPattern001
  Angle = 360
  Axis = -> Sketch021 [N_Axis]
  BaseFeature = -> Pocket006
  Occurrences = 4
  Originals = -> [Pocket006]
FEATURE [PartDesign::Pocket] Pocket007  label="bottom_hole_Pocket007"
  BaseFeature = -> PolarPattern001
  Length = 5
  Length2 = 100
  Profile = -> Sketch024
  Refine = true
  Type = 1
FEATURE [PartDesign::PolarPattern] PolarPattern004
  Angle = 360
  Axis = -> Sketch [N_Axis]
  BaseFeature = -> Pad004
  Occurrences = 4
  Originals = -> [Pad004]
FEATURE [PartDesign::Hole] Hole002
  BaseFeature = -> PolarPattern004
  Depth = 25
  DepthType = 0
  Diameter = 3.3
  DrillPoint = 1
  DrillPointAngle = 118
  HoleCutCountersinkAngle = 90
  HoleCutDepth = 0
  HoleCutDiameter = 3
  HoleCutType = 0
  ModelActualThread = false
  Profile = -> Sketch018
  Tapered = false
  TaperedAngle = 90
  ThreadAngle = 0
  ThreadClass = 0
  ThreadCutOffInner = 0
  ThreadCutOffOuter = 0
  ThreadDirection = 0
  ThreadFit = 0
  ThreadPitch = 0
  ThreadSize = 3
  ThreadType = 1
  Threaded = false
FEATURE [PartDesign::Boolean] Boolean
  BaseFeature = -> Hole002
  Group = -> [Body004026]
  Refine = true
  Type = 1
FEATURE [PartDesign::Body] Body  label="crystal_mounting_layer_1_Body"
  Group = -> [Pad004,PolarPattern004,Hole002,Boolean]
  Origin = -> Origin021
  Tip = -> Boolean
FEATURE [TechDraw::DrawViewPart] View002
  CoarseView = false
  Direction = (0,0,1)
  Focus = 100
  HardHidden = false
  IsoCount = 0
  IsoHidden = false
  IsoVisible = false
  LockPosition = false
  Perspective = false
  Rotation = 0
  ScaleType = 0
  SeamHidden = false
  SeamVisible = false
  SmoothHidden = false
  SmoothVisible = false
  Source = -> [Body]
  X = 148.5
  Y = 105
FEATURE [TechDraw::DrawPage] Page002  label="crystal_mounting_layer1_Page"
  KeepUpdated = true
  ProjectionType = 0
  Template = -> Template002
  Views = -> [View002]
FEATURE [PartDesign::PolarPattern] PolarPattern005
  Angle = 360
  Axis = -> Sketch [N_Axis]
  BaseFeature = -> Pad005
  Occurrences = 4
  Originals = -> [Pad005]
  Refine = true
FEATURE [PartDesign::Boolean] Boolean001
  BaseFeature = -> PolarPattern005
  Group = -> [Body004025]
  Type = 1
FEATURE [PartDesign::Hole] Hole001
  BaseFeature = -> Boolean001
  Depth = 25
  DepthType = 1
  Diameter = 3.3
  DrillPoint = 0
  DrillPointAngle = 118
  HoleCutCountersinkAngle = 90
  HoleCutDepth = 1.8
  HoleCutDiameter = 6
  HoleCutType = 1
  ModelActualThread = false
  Profile = -> Sketch018
  Refine = true
  Tapered = false
  TaperedAngle = 90
  ThreadAngle = 60
  ThreadClass = 0
  ThreadCutOffInner = 0.0541266
  ThreadCutOffOuter = 0.108253
  ThreadDirection = 0
  ThreadFit = 0
  ThreadPitch = 0.5
  ThreadSize = 3
  ThreadType = 1
  Threaded = false
FEATURE [PartDesign::Body] Body004006  label="crystal_mounting_layer_2_Body"
  Group = -> [Pad005,PolarPattern005,Boolean001,Hole001]
  Origin = -> Origin022
  Placement = pos=(0,0,4) rot=(0,0,1;0rad)
  Tip = -> Hole001
FEATURE [TechDraw::DrawViewPart] View003
  CoarseView = false
  Direction = (0,0,1)
  Focus = 100
  HardHidden = false
  IsoCount = 0
  IsoHidden = false
  IsoVisible = false
  LockPosition = false
  Perspective = false
  Rotation = 0
  ScaleType = 0
  SeamHidden = false
  SeamVisible = false
  SmoothHidden = false
  SmoothVisible = false
  Source = -> [Body004006]
  X = 148.5
  Y = 105
FEATURE [TechDraw::DrawPage] Page003  label="crystal_mounting_layer2_Page"
  KeepUpdated = true
  ProjectionType = 0
  Template = -> Template003
  Views = -> [View003]
FEATURE [TechDraw::DrawViewPart] View008  label="crystal_mounting_layer_1_View008"
  Caption = crystal_layer_1
  CoarseView = false
  Direction = (0,0,1)
  Focus = 100
  HardHidden = false
  IsoCount = 0
  IsoHidden = false
  IsoVisible = false
  LockPosition = true
  Perspective = false
  Rotation = 0
  ScaleType = 0
  SeamHidden = false
  SeamVisible = false
  SmoothHidden = false
  SmoothVisible = false
  Source = -> [Body]
  X = 150
  Y = 165
FEATURE [TechDraw::DrawViewPart] View009  label="crystal_mounting_layer_2_View009"
  Caption = crystal_layer_2
  CoarseView = false
  Direction = (0,0,1)
  Focus = 100
  HardHidden = false
  IsoCount = 0
  IsoHidden = false
  IsoVisible = false
  LockPosition = true
  Perspective = false
  Rotation = 0
  ScaleType = 0
  SeamHidden = false
  SeamVisible = false
  SmoothHidden = false
  SmoothVisible = false
  Source = -> [Body004006]
  X = 96
  Y = 165
FEATURE [TechDraw::DrawViewPart] View010  label="lightguide_mounting_View010"
  Caption = lightguide_mounting
  CoarseView = false
  Direction = (0,0,1)
  Focus = 100
  HardHidden = false
  IsoCount = 0
  IsoHidden = false
  IsoVisible = false
  LockPosition = true
  Perspective = false
  Rotation = 0
  ScaleType = 0
  SeamHidden = false
  SeamVisible = false
  SmoothHidden = false
  SmoothVisible = false
  Source = -> [Body004008]
  X = 204
  Y = 165
FEATURE [TechDraw::DrawViewPart] View011  label="light_blocker_View011"
  CoarseView = false
  Direction = (0.94,0.342,0)
  Focus = 100
  HardHidden = false
  IsoCount = 0
  IsoHidden = false
  IsoVisible = false
  LockPosition = true
  Perspective = false
  Rotation = 0
  ScaleType = 0
  SeamHidden = false
  SeamVisible = false
  SmoothHidden = false
  SmoothVisible = false
  Source = -> [Mirrored001]
  X = 25
  Y = 46
FEATURE [TechDraw::DrawViewDimension] Dimension
  Arbitrary = false
  FormatSpec = %.3f
  LockPosition = false
  MeasureType = 1
  OverTolerance = 0
  References2D = -> [View011]
  Rotation = 0
  ScaleType = 0
  Type = 2
  UnderTolerance = 0
  X = 9.45135
  Y = 1.56373
FEATURE [TechDraw::DrawViewDimension] Dimension001
  Arbitrary = false
  FormatSpec = %.3f
  LockPosition = false
  MeasureType = 1
  OverTolerance = 0
  References2D = -> [View011]
  Rotation = 0
  ScaleType = 0
  Type = 1
  UnderTolerance = 0
  X = 0.380567
  Y = -28.3583
FEATURE [TechDraw::DrawViewPart] View013  label="light_blocker_View013"
  CoarseView = false
  Direction = (0.94,0.342,0)
  Focus = 100
  HardHidden = false
  IsoCount = 0
  IsoHidden = false
  IsoVisible = false
  LockPosition = true
  Perspective = false
  Rotation = 0
  ScaleType = 0
  SeamHidden = false
  SeamVisible = false
  SmoothHidden = false
  SmoothVisible = false
  Source = -> [Mirrored001]
  X = 50
  Y = 46
FEATURE [TechDraw::DrawViewPart] View014  label="light_blocker_View014"
  CoarseView = false
  Direction = (0.94,0.342,0)
  Focus = 100
  HardHidden = false
  IsoCount = 0
  IsoHidden = false
  IsoVisible = false
  LockPosition = true
  Perspective = false
  Rotation = 0
  ScaleType = 0
  SeamHidden = false
  SeamVisible = false
  SmoothHidden = false
  SmoothVisible = false
  Source = -> [Mirrored001]
  X = 77
  Y = 46
FEATURE [TechDraw::DrawViewPart] View015  label="light_blocker_View015"
  CoarseView = false
  Direction = (0.94,0.342,0)
  Focus = 100
  HardHidden = false
  IsoCount = 0
  IsoHidden = false
  IsoVisible = false
  LockPosition = true
  Perspective = false
  Rotation = 0
  ScaleType = 0
  SeamHidden = false
  SeamVisible = false
  SmoothHidden = false
  SmoothVisible = false
  Source = -> [Mirrored001]
  X = 100
  Y = 46
FEATURE [Sketcher::SketchObject] Sketch028  label="mounting_outline_round_Sketch"
  MapMode = 5
  Support = -> [XY_Plane023]
  expr: Constraints[1] = data.mounting_outline_radius
  sketch-geometry (1):
    g0: Circle CenterX=0 CenterY=0 CenterZ=0 NormalX=0 NormalY=0 NormalZ=1 AngleXU=0 Radius=26
  constraints (2):
    c: Coincident(g0,g-1)
    c: Radius(g0) = 26
FEATURE [PartDesign::Body] Body004007  label="mounting_helper_Body"
  Group = -> [Sketch,Sketch014,ShapeBinder004,Sketch018,Sketch021,Sketch027,Sketch028]
  Origin = -> Origin023
FEATURE [PartDesign::Pad] Pad012
  Length = 1
  Length2 = 100
  Profile = -> Sketch028
  Type = 0
  expr: Length = data.wood2_thickness
FEATURE [PartDesign::FeatureBase] Clone023
  BaseFeature = -> Body001001
FEATURE [PartDesign::Body] Body004031  label="crystal_Clone4"
  Group = -> [Clone023]
  Origin = -> Origin051
  Placement = pos=(0,0,-12) rot=(0,0,1;0rad)
  Tip = -> Clone023
  expr: Placement.Base.z = data.crystal_mounting_fit_offset - (data.wood_thickness * 2 + data.wood3_thickness)
FEATURE [PartDesign::Boolean] Boolean002
  BaseFeature = -> Pad012
  Group = -> [Body004031]
  Type = 1
FEATURE [PartDesign::Body] Body004030  label="crystal_mounting_layer_4_Body"
  Group = -> [Pad012,Boolean002]
  Origin = -> Origin050
  Placement = pos=(0,0,11) rot=(0,0,1;0rad)
  Tip = -> Boolean002
  expr: Placement.Base.z = data.wood_thickness * 2 + data.wood3_thickness
FEATURE [TechDraw::DrawSVGTemplate] Template008
  Height = 210
  Orientation = 1
  Width = 297
FEATURE [TechDraw::DrawViewPart] View017  label="layer3_view"
  CoarseView = false
  Direction = (0,0,1)
  Focus = 100
  HardHidden = false
  IsoCount = 0
  IsoHidden = false
  IsoVisible = false
  LockPosition = false
  Perspective = false
  Rotation = 0
  ScaleType = 0
  SeamHidden = false
  SeamVisible = false
  SmoothHidden = false
  SmoothVisible = false
  Source = -> [Body004030]
  X = 148.5
  Y = 105
FEATURE [TechDraw::DrawPage] Page008  label="crystal_mounting_layer4_Page"
  KeepUpdated = true
  ProjectionType = 0
  Template = -> Template008
  Views = -> [View017]
FEATURE [TechDraw::DrawViewPart] View018  label="crystal_mounting_layer_3_View"
  Caption = crystal_layer_3
  CoarseView = false
  Direction = (0,0,1)
  Focus = 100
  HardHidden = false
  IsoCount = 0
  IsoHidden = false
  IsoVisible = false
  LockPosition = true
  Perspective = false
  Rotation = 0
  ScaleType = 0
  SeamHidden = false
  SeamVisible = false
  SmoothHidden = false
  SmoothVisible = false
  Source = -> [Body004030]
  X = 40
  Y = 165
FEATURE [PartDesign::Fillet] Fillet
  Base = -> Pocket007 [Edge72,Edge70,Edge75,Edge74]
  BaseFeature = -> Pocket007
  Radius = 2
FEATURE [PartDesign::Body] Body004024  label="bottom_Body"
  Group = -> [Pad009,PolarPattern003,Hole003,Pocket006,PolarPattern001,Sketch024,Pocket007,Fillet]
  Origin = -> Origin044
  Placement = pos=(0,0,-40) rot=(0,0,1;0rad)
  Tip = -> Fillet
  expr: Placement.Base.z = (data.lightblocker_side_height - data.wood_thickness) * -1
FEATURE [TechDraw::DrawViewPart] View005
  CoarseView = false
  Direction = (0,0,1)
  Focus = 100
  HardHidden = false
  IsoCount = 0
  IsoHidden = false
  IsoVisible = false
  LockPosition = false
  Perspective = false
  Rotation = 0
  ScaleType = 0
  SeamHidden = false
  SeamVisible = false
  SmoothHidden = false
  SmoothVisible = false
  Source = -> [Body004024]
  X = 148.5
  Y = 105
FEATURE [TechDraw::DrawPage] Page006  label="bottom_Page"
  KeepUpdated = true
  ProjectionType = 0
  Template = -> Template006
  Views = -> [View005]
FEATURE [TechDraw::DrawViewPart] View016  label="bottom_View016"
  Caption = bottom
  CoarseView = false
  Direction = (0,0,1)
  Focus = 100
  HardHidden = false
  IsoCount = 0
  IsoHidden = false
  IsoVisible = false
  LockPosition = true
  Perspective = false
  Rotation = 0
  ScaleType = 0
  SeamHidden = false
  SeamVisible = false
  SmoothHidden = false
  SmoothVisible = false
  Source = -> [Body004024]
  X = 258
  Y = 165
FEATURE [TechDraw::DrawPage] Page007  label="drawing_mountings_Page"
  KeepUpdated = true
  ProjectionType = 0
  Template = -> Template007
  Views = -> [View008,View009,View010,View011,Dimension,Dimension001,View013,View014,View015,View016,View018]
FEATURE [App::DocumentObjectGroup] Group002  label="drawings_mounting"
  Group = -> [Page007]
FEATURE [TechDraw::DrawViewPart] View019
  CoarseView = false
  Direction = (0.819,0.574,0)
  Focus = 100
  HardHidden = false
  IsoCount = 0
  IsoHidden = false
  IsoVisible = false
  LockPosition = false
  Perspective = false
  Rotation = 0
  ScaleType = 0
  SeamHidden = false
  SeamVisible = false
  SmoothHidden = false
  SmoothVisible = false
  Source = -> [Mirrored001]
  X = 148.5
  Y = 105
FEATURE [TechDraw::DrawPage] Page005  label="lightblocker_side_Page"
  KeepUpdated = true
  ProjectionType = 0
  Template = -> Template005
  Views = -> [View019]
FEATURE [TechDraw::DrawSVGTemplate] Template009
  Height = 210
  Orientation = 1
  Width = 297
FEATURE [PartDesign::Pad] Pad013
  Length = 3
  Length2 = 100
  Profile = -> Sketch028
  Type = 0
  expr: Length = data.wood3_thickness
FEATURE [PartDesign::FeatureBase] Clone024
  BaseFeature = -> Body001001
FEATURE [PartDesign::Body] Body004033  label="crystal_clone3"
  Group = -> [Clone024]
  Origin = -> Origin053
  Placement = pos=(0,0,-9) rot=(0,0,1;0rad)
  Tip = -> Clone024
  expr: Placement.Base.z = data.crystal_mounting_fit_offset - data.wood_thickness * 2
FEATURE [PartDesign::Boolean] Boolean003
  BaseFeature = -> Pad013
  Group = -> [Body004033]
  Type = 1
FEATURE [PartDesign::Hole] Hole005
  BaseFeature = -> Boolean003
  Depth = 25
  DepthType = 1
  Diameter = 3.3
  DrillPoint = 0
  DrillPointAngle = 118
  HoleCutCountersinkAngle = 90
  HoleCutDepth = 10
  HoleCutDiameter = 6
  HoleCutType = 1
  ModelActualThread = false
  Profile = -> Sketch018
  Tapered = false
  TaperedAngle = 90
  ThreadAngle = 0
  ThreadClass = 0
  ThreadCutOffInner = 0
  ThreadCutOffOuter = 0
  ThreadDirection = 0
  ThreadFit = 0
  ThreadPitch = 0
  ThreadSize = -1
  ThreadType = 0
  Threaded = false
FEATURE [PartDesign::Body] Body004032  label="crystal_mounting_layer_3_Body"
  Group = -> [Pad013,Boolean003,Hole005]
  Origin = -> Origin052
  Placement = pos=(0,0,8) rot=(0,0,1;0rad)
  Tip = -> Hole005
FEATURE [TechDraw::DrawViewPart] View020
  CoarseView = false
  Direction = (0,0,1)
  Focus = 100
  HardHidden = false
  IsoCount = 0
  IsoHidden = false
  IsoVisible = false
  LockPosition = false
  Perspective = false
  Rotation = 0
  ScaleType = 0
  SeamHidden = false
  SeamVisible = false
  SmoothHidden = false
  SmoothVisible = false
  Source = -> [Body004032]
  X = 148.5
  Y = 105
FEATURE [TechDraw::DrawPage] Page009  label="crystal_mounting_layer3_Page"
  KeepUpdated = true
  ProjectionType = 0
  Template = -> Template009
  Views = -> [View020]
FEATURE [App::DocumentObjectGroup] Group001  label="export_mounting"
  Group = -> [Page002,Page003,Page004,Page005,Page006,Page008,Page009]
FEATURE [App::Part] Part007  label="mounting_Part"
  Group = -> [Body,Body004006,Body004007,Body004008,Body004020,Body004021,Body004022,Body004023,Body004024,Group001,Page002,Page003,Page004,Page005,Page006,Group002,Page007,Body004027,Body004028,Body004029,Body004030,Page008,Page009,Body004032]
  Origin = -> Origin020
